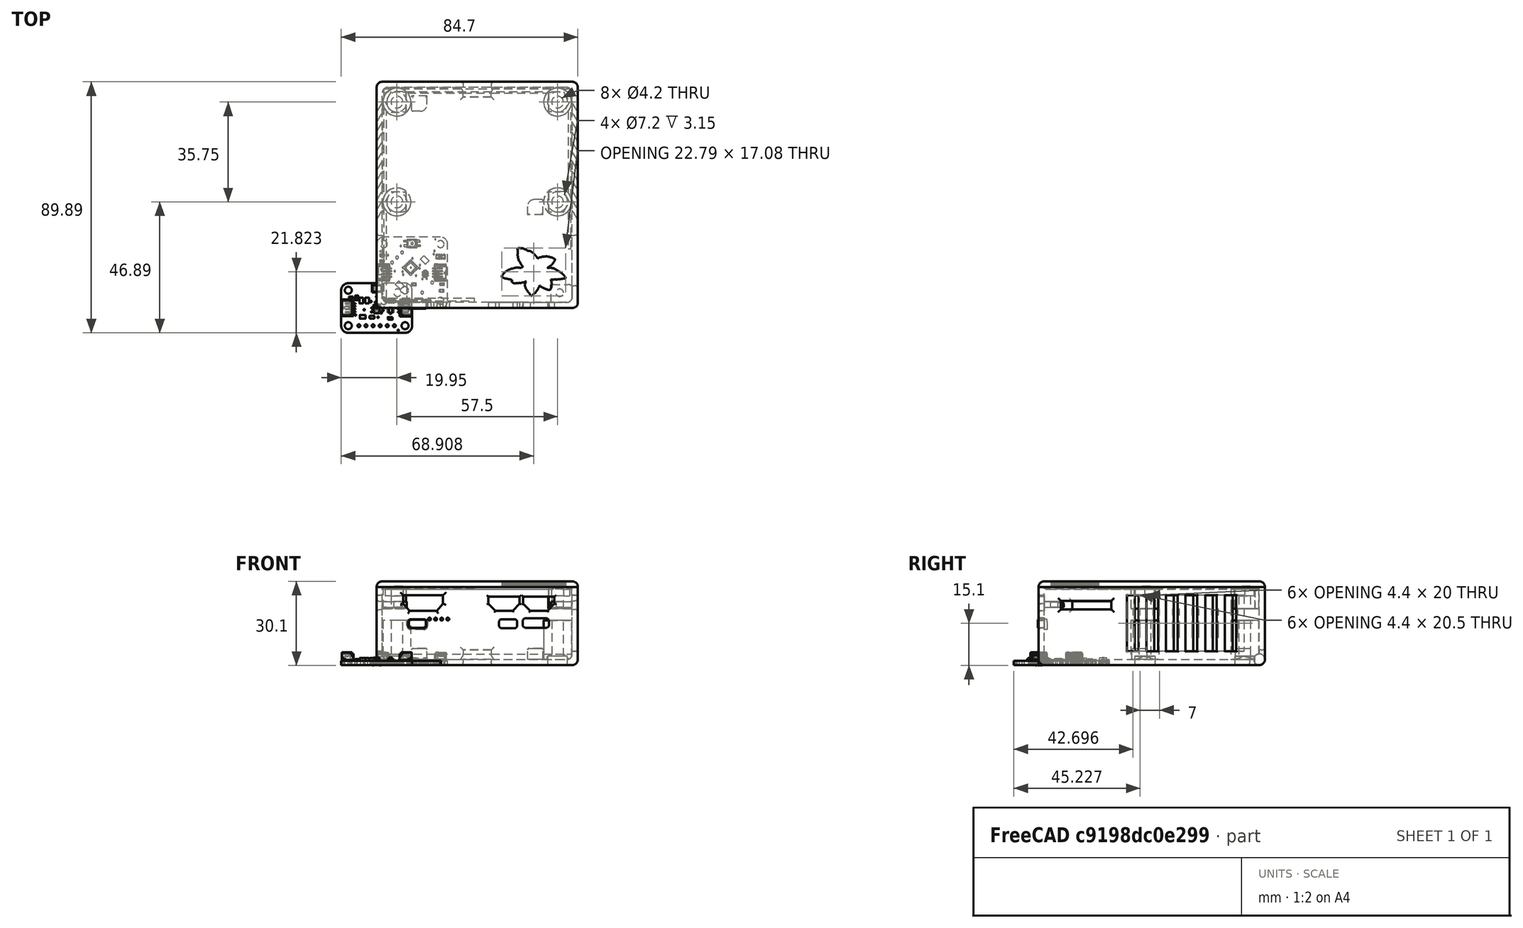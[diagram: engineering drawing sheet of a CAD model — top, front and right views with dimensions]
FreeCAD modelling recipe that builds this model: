
FCSTD DOCUMENT  (FreeCAD 0.20R29410 (Git))
Label: wearableV5_April_11_2023
License: All rights reserved
LicenseURL: http://en.wikipedia.org/wiki/All_rights_reserved
objects: Part::Feature×60, Part::Cylinder×20, Part::MultiFuse×16, Sketcher::SketchObject×15, Part::Extrusion×15, Part::Fillet×14, App::Part×9, Part::Box×5, Mesh::Feature×5, Part::Cut×4, Part::Compound×1
note: 150 computed .brp shape members not serialized (recipe doc carries the construction recipe); baked Part::Feature solids carry a one-line shape summary decoded from their .brp

FEATURE [Part::Box] Box  label="battery"
  AttacherType = Attacher::AttachEngine3D
  Height = 11
  Length = 65
  Placement = pos=(4,2,2) rot=(0,0,1;0rad)
  Width = 30
FEATURE [Mesh::Feature] pisugar3Board
  Placement = pos=(-2.89,35.08,0.25) rot=(-1,0,0;4.71239rad)
FEATURE [Part::Feature] Part__Feature001  label="RaspberryPiZeroW"
  Placement = pos=(36.5,17,19.18) rot=(1,0,0;1.5708rad)
  shape: bbox 65.9 x 31.25 x 4.8 mm, 368 faces, 2 solids (baked)
FEATURE [Part::Feature] Part__Feature  label="ips7100"
  Placement = pos=(-24,0,222) rot=(0.999993,-0.003655,0;3.14159rad)
  shape: bbox 48.14 x 14.05 x 44.14 mm, 1935 faces (baked)
FEATURE [Part::Compound] Compound  label="ips7100s"
  Links = -> [Part__Feature]
  Placement = pos=(12.15,32.5,15.79) rot=(0,0.707107,0.707107;3.15032rad)
FEATURE [Part::Feature] Part__Feature002  label="Printed Circuit Board"
  shape: bbox 25.4 x 17.78 x 1.6 mm, 42 faces (baked)
FEATURE [Part::Feature] Part__Feature003  label="EAHC2835WD6"
  shape: bbox 3.513 x 2.813 x 0.7485 mm, 108 faces, 4 solids (baked)
FEATURE [Part::Feature] Part__Feature004  label="AS7341 v2"
  Placement = pos=(0,-0.339822,1.6) rot=(0,0,1;0rad)
  shape: bbox 2 x 3.1 x 1.1 mm, 267 faces, 26 solids (baked)
FEATURE [Part::Feature] Part__Feature005  label="CAPC-0805-T0.95-BN v1"
  Placement = pos=(-5.01759,-3.15294,1.6) rot=(0,0,1;0rad)
  shape: bbox 2.1 x 1.35 x 0.95 mm, 42 faces (baked)
FEATURE [Part::Feature] Part__Feature006  label="CAPC-0805-T0.95-BN v002"
  Placement = pos=(-5.48627,2.66154,1.6) rot=(0,0,-1;1.5708rad)
  shape: bbox 1.35 x 2.1 x 0.95 mm, 42 faces (baked)
FEATURE [Part::Feature] Part__Feature007  label="CAPC-0805-T0.95-BN v003"
  Placement = pos=(-3.43627,2.66154,1.6) rot=(0,0,-1;1.5708rad)
  shape: bbox 1.35 x 2.1 x 0.95 mm, 42 faces (baked)
FEATURE [Part::Feature] Part__Feature008  label="CAPC-0603-T0.9-BN v1"
  Placement = pos=(-1.69987,-3.28475,1.6) rot=(0,0,1;0rad)
  shape: bbox 1.7 x 0.9 x 0.9 mm, 42 faces (baked)
FEATURE [Part::Feature] Part__Feature009  label="BODY_MF06A"
  Placement = pos=(0,0,0.762) rot=(0.57735,-0.57735,-0.57735;2.0944rad)
  shape: bbox 1.601 x 2.921 x 1.016 mm, 42 faces (baked)
FEATURE [Part::Feature] Part__Feature010  label="LEAD_MF06A"
  Placement = pos=(-0.9652,-0.9525,0.1016) rot=(0.57735,-0.57735,-0.57735;2.0944rad)
  shape: bbox 0.6223 x 0.3749 x 0.8636 mm, 14 faces (baked)
FEATURE [Part::Feature] Part__Feature011  label="LEAD_MF06A001"
  Placement = pos=(-0.9652,0,0.1016) rot=(0.57735,-0.57735,-0.57735;2.0944rad)
  shape: bbox 0.6223 x 0.3749 x 0.8636 mm, 14 faces (baked)
FEATURE [Part::Feature] Part__Feature012  label="LEAD_MF06A002"
  Placement = pos=(-0.9652,0.9525,0.1016) rot=(0.57735,-0.57735,-0.57735;2.0944rad)
  shape: bbox 0.6223 x 0.3749 x 0.8636 mm, 14 faces (baked)
FEATURE [Part::Feature] Part__Feature013  label="LEAD_MF06A003"
  Placement = pos=(0.9652,-0.9525,0.1016) rot=(0.57735,0.57735,0.57735;2.0944rad)
  shape: bbox 0.6223 x 0.3749 x 0.8636 mm, 14 faces (baked)
FEATURE [Part::Feature] Part__Feature014  label="LEAD_MF06A004"
  Placement = pos=(0.9652,0,0.1016) rot=(0.57735,0.57735,0.57735;2.0944rad)
  shape: bbox 0.6223 x 0.3749 x 0.8636 mm, 14 faces (baked)
FEATURE [Part::Feature] Part__Feature015  label="LEAD_MF06A005"
  Placement = pos=(0.9652,0.9525,0.1016) rot=(0.57735,0.57735,0.57735;2.0944rad)
  shape: bbox 0.6223 x 0.3749 x 0.8636 mm, 14 faces (baked)
FEATURE [Part::Feature] Part__Feature016  label="SOT363 v2"
  Placement = pos=(4.97054,-0.645171,1.675) rot=(0,0,1;3.14159rad)
  shape: bbox 2.1 x 2 x 1.1 mm, 94 faces, 7 solids (baked)
FEATURE [Part::Feature] Part__Feature017  label="LED 0603 single color v1"
  Placement = pos=(-9.18406,3.72778,1.60762) rot=(0,0,1;1.5708rad)
  shape: bbox 1.961 x 0.7932 x 0.7145 mm, 63 faces, 5 solids (baked)
FEATURE [Part::Feature] Part__Feature018  label="RESC-0603 v1"
  Placement = pos=(4.83432,-3.67461,1.6) rot=(0,0,1;0rad)
  shape: bbox 1.7 x 0.9 x 0.55 mm, 52 faces, 3 solids (baked)
FEATURE [Part::Feature] Part__Feature019  label="RESC-0603 v002"
  Placement = pos=(-7.14949,3.61248,1.6) rot=(0,0,-1;1.5708rad)
  shape: bbox 0.9 x 1.7 x 0.55 mm, 52 faces, 3 solids (baked)
FEATURE [Part::Feature] Part__Feature020  label="YC164_RESPACK v1"
  Placement = pos=(2.99591,1.52916,1.6) rot=(0,0,1;0rad)
  shape: bbox 3.2 x 1.6 x 0.61 mm, 172 faces (baked)
FEATURE [Part::Feature] Part__Feature021  label="qwicc v2"
  Placement = pos=(-10.8364,0.0607456,1.65) rot=(0,0,-1;1.5708rad)
  shape: bbox 4.95 x 6 x 2.96 mm, 229 faces, 7 solids (baked)
FEATURE [Part::Feature] Part__Feature022  label="qwicc v003"
  Placement = pos=(10.8256,0.00556102,1.65) rot=(0,0,1;1.5708rad)
  shape: bbox 4.95 x 6 x 2.96 mm, 229 faces, 7 solids (baked)
FEATURE [Part::Feature] Part__Feature023  label="scd30"
  Placement = pos=(20,54,27) rot=(0.57735,0.57735,-0.57735;4.18879rad)
  shape: bbox 23.02 x 35.11 x 7.027 mm, 2292 faces, 25 solids (baked)
FEATURE [App::Part] sot_23_6_v2  label="sot-23-6 v2"
  Group = -> [Part__Feature009,Part__Feature010,Part__Feature011,Part__Feature012,Part__Feature013,Part__Feature014,Part__Feature015]
  Origin = -> Origin
  Placement = pos=(-4.47945,-0.603742,1.69152) rot=(0,0,1;0rad)
FEATURE [App::Part] Adafruit_AS7341_STEMMA_QT_v2  label="bme280"
  Group = -> [Part__Feature002,Part__Feature003,Part__Feature004,Part__Feature005,Part__Feature006,Part__Feature007,Part__Feature008,sot_23_6_v2,Part__Feature016,Part__Feature017,Part__Feature018,Part__Feature019,Part__Feature020,Part__Feature021,Part__Feature022]
  Origin = -> Origin001
  Placement = pos=(47.7,42,20) rot=(0,0,1;0rad)
FEATURE [Part::Box] Box002  label="bottom"
  AttacherType = Attacher::AttachEngine3D
  Height = 28
  Length = 72
  Width = 81
FEATURE [Part::Fillet] Fillet  label="bottom002"
  Base = -> Box002
  Edges = 8 edges r=2: [Edge1,Edge3,Edge4,Edge5,Edge7,Edge8,Edge9,Edge11]
FEATURE [Part::Box] Box003  label="bottom001"
  AttacherType = Attacher::AttachEngine3D
  Height = 39
  Length = 68
  Placement = pos=(2,2,2) rot=(0,0,1;0rad)
  Width = 77
FEATURE [Part::Fillet] Fillet001  label="bottomCut"
  Base = -> Box003
  Edges = 8 edges r=2: [Edge1,Edge3,Edge4,Edge5,Edge7,Edge8,Edge9,Edge11]
FEATURE [Part::Cut] Cut  label="bottom003"
  Base = -> Fillet
  Tool = -> Fillet001
FEATURE [Part::Cylinder] Cylinder
  Angle = 360
  AttacherType = Attacher::AttachEngine3D
  FirstAngle = 0
  Height = 14
  Placement = pos=(7.25,73.75,2) rot=(0,0,1;0rad)
  Radius = 5
  SecondAngle = 0
FEATURE [Part::Cylinder] Cylinder001
  Angle = 360
  AttacherType = Attacher::AttachEngine3D
  FirstAngle = 0
  Height = 14
  Placement = pos=(64.75,38,2) rot=(0,0,1;0rad)
  Radius = 5
  SecondAngle = 0
FEATURE [Part::Cylinder] Cylinder002
  Angle = 360
  AttacherType = Attacher::AttachEngine3D
  FirstAngle = 0
  Height = 14
  Placement = pos=(7.25,38,2) rot=(0,0,1;0rad)
  Radius = 5
  SecondAngle = 0
FEATURE [Part::Cylinder] Cylinder003
  Angle = 360
  AttacherType = Attacher::AttachEngine3D
  FirstAngle = 0
  Height = 14
  Placement = pos=(64.75,73.75,2) rot=(0,0,1;0rad)
  Radius = 5
  SecondAngle = 0
FEATURE [Part::MultiFuse] Fusion  label="basesBottomIn"
  Shapes = -> [Cylinder003,Cylinder,Cylinder001,Cylinder002]
FEATURE [Part::Feature] Part__Feature024  label="Board"
  shape: bbox 25.4 x 25.4 x 1.57 mm, 211 faces (baked)
FEATURE [Part::Feature] Part__Feature025  label="QFN24_4MM"
  Placement = pos=(12.1412,14.4526,1.57) rot=(0,0,1;3.92699rad)
  shape: bbox 5.657 x 5.657 x 0.9 mm, 172 faces (baked)
FEATURE [Part::Feature] Part__Feature026  label="Part 5"
  shape: bbox 0.48 x 0.6603 x 0.6 mm, 14 faces (baked)
FEATURE [Part::Feature] Part__Feature027  label="Part 6"
  shape: bbox 0.48 x 0.6603 x 0.6 mm, 14 faces (baked)
FEATURE [Part::Feature] Part__Feature028  label="Part 4"
  shape: bbox 0.48 x 0.6603 x 0.6 mm, 14 faces (baked)
FEATURE [Part::Feature] Part__Feature029  label="Part 3"
  shape: bbox 0.48 x 0.6603 x 0.6 mm, 14 faces (baked)
FEATURE [Part::Feature] Part__Feature030  label="Part 2"
  shape: bbox 0.48 x 0.6603 x 0.6 mm, 14 faces (baked)
FEATURE [Part::Feature] Part__Feature031  label="Part 1"
  shape: bbox 3 x 1.4 x 1 mm, 10 faces (baked)
FEATURE [App::Part] _6700497  label="36700497"
  Group = -> [Part__Feature026,Part__Feature027,Part__Feature028,Part__Feature029,Part__Feature030,Part__Feature031]
  Origin = -> Origin002
  Placement = pos=(0,0,0) rot=(0,0,1;3.14159rad)
FEATURE [App::Part] SOT23_5  label="SOT23-5"
  Group = -> [_6700497]
  Origin = -> Origin003
  Placement = pos=(2.54,6.985,1.57) rot=(0,0,1;3.14159rad)
FEATURE [Part::Feature] Part__Feature032  label="Pin1"
  shape: bbox 0.6224 x 1.252 x 1.252 mm, 37 faces (baked)
FEATURE [Part::Feature] Part__Feature033  label="Pin2"
  shape: bbox 0.6224 x 1.252 x 1.252 mm, 37 faces (baked)
FEATURE [Part::Feature] Part__Feature034  label="CeramicBody"
  shape: bbox 1.8 x 1.23 x 1.23 mm, 10 faces (baked)
FEATURE [App::Part] _603_NO  label="0603-NO"
  Group = -> [Part__Feature032,Part__Feature033,Part__Feature034]
  Origin = -> Origin004
  Placement = pos=(16.51,8.382,1.57) rot=(0,0,1;0rad)
FEATURE [Part::Feature] Part__Feature035  label="0603-NO (1)"
  Placement = pos=(23.241,6.223,1.57) rot=(0,0,1;0rad)
  shape: bbox 1.7 x 0.9 x 0.55 mm, 52 faces, 3 solids (baked)
FEATURE [Part::Feature] Part__Feature036  label="0603-NO (2)"
  Placement = pos=(13.3858,8.4328,1.57) rot=(0,0,1;0rad)
  shape: bbox 1.7 x 0.9 x 0.55 mm, 52 faces, 3 solids (baked)
FEATURE [Part::Feature] Part__Feature037  label="0603-NO (3)"
  Placement = pos=(1.905,18.923,1.57) rot=(0,0,1;3.14159rad)
  shape: bbox 1.7 x 0.9 x 0.55 mm, 52 faces, 3 solids (baked)
FEATURE [Part::Feature] Part__Feature038  label="Pin1 (1)"
  shape: bbox 0.6224 x 1.252 x 1.252 mm, 37 faces (baked)
FEATURE [Part::Feature] Part__Feature039  label="Pin2 (1)"
  shape: bbox 0.6224 x 1.252 x 1.252 mm, 37 faces (baked)
FEATURE [Part::Feature] Part__Feature040  label="CeramicBody (1)"
  shape: bbox 1.8 x 1.23 x 1.23 mm, 10 faces (baked)
FEATURE [App::Part] _805_NO  label="0805-NO"
  Group = -> [Part__Feature038,Part__Feature039,Part__Feature040]
  Origin = -> Origin005
  Placement = pos=(7.874,13.589,1.57) rot=(0,0,1;1.5708rad)
FEATURE [Part::Feature] Part__Feature041  label="Pin1 (2)"
  shape: bbox 0.6224 x 1.252 x 1.252 mm, 37 faces (baked)
FEATURE [Part::Feature] Part__Feature042  label="Pin2 (2)"
  shape: bbox 0.6224 x 1.252 x 1.252 mm, 37 faces (baked)
FEATURE [Part::Feature] Part__Feature043  label="CeramicBody (2)"
  shape: bbox 1.8 x 1.23 x 1.23 mm, 10 faces (baked)
FEATURE [App::Part] _805_NO__1_  label="0805-NO (1)"
  Group = -> [Part__Feature041,Part__Feature042,Part__Feature043]
  Origin = -> Origin006
  Placement = pos=(12.827,6.223,1.57) rot=(0,0,1;3.14159rad)
FEATURE [Part::Feature] Part__Feature044  label="CHIPLED_0603_NOOUTLINE"
  Placement = pos=(23.368,8.509,1.57) rot=(0,0,1;1.5708rad)
  shape: bbox 1.616 x 0.8 x 0.4 mm, 133 faces (baked)
FEATURE [Part::Feature] Part__Feature045  label="CHIPLED_0603_NOOUTLINE (1)"
  Placement = pos=(1.905,16.764,1.57) rot=(0,0,-1;1.5708rad)
  shape: bbox 1.616 x 0.8 x 0.4 mm, 133 faces (baked)
FEATURE [Part::Feature] Part__Feature046  label="JST_SH4"
  Placement = pos=(22.86,12.7,1.57) rot=(0,0,1;1.5708rad)
  shape: bbox 4.95 x 6 x 2.96 mm, 229 faces, 7 solids (baked)
FEATURE [Part::Feature] Part__Feature047  label="JST_SH4 (1)"
  Placement = pos=(2.54,12.7,1.57) rot=(0,0,-1;1.5708rad)
  shape: bbox 4.95 x 6 x 2.96 mm, 229 faces, 7 solids (baked)
FEATURE [Part::Feature] Part__Feature048  label="NEO3535_REVERSE"
  Placement = pos=(12.7,23.114,0) rot=(0,1,0;3.14159rad)
  shape: bbox 5.88 x 2.8 x 1.78 mm, 41 faces, 5 solids (baked)
FEATURE [Part::Feature] Part__Feature049  label="RESPACK_4X0603"
  Placement = pos=(22.86,18.415,1.57) rot=(0,0,1;3.14159rad)
  shape: bbox 3.2 x 1.6 x 0.61 mm, 172 faces (baked)
FEATURE [Part::Feature] Part__Feature050  label="SOT363"
  Placement = pos=(17.399,12.192,1.57) rot=(0,0,-1;1.5708rad)
  shape: bbox 2.208 x 2.208 x 1.121 mm, 178 faces, 4 solids (baked)
FEATURE [App::Part] Packages
  Group = -> [Part__Feature025,SOT23_5,_603_NO,Part__Feature035,Part__Feature036,Part__Feature037,_805_NO,_805_NO__1_,Part__Feature044,Part__Feature045,Part__Feature046,Part__Feature047,Part__Feature048,Part__Feature049,Part__Feature050]
  Origin = -> Origin007
FEATURE [App::Part] Adafruit_I2C_QT_Rotary_Encoder_v2  label="gps"
  Group = -> [Part__Feature024,Packages]
  Origin = -> Origin008
  Placement = pos=(35,51,20) rot=(0,0,1;0rad)
FEATURE [Part::Cylinder] Cylinder004
  Angle = 360
  AttacherType = Attacher::AttachEngine3D
  FirstAngle = 0
  Height = 14
  Placement = pos=(7.25,73.75,2) rot=(0,0,1;0rad)
  Radius = 2.1
  SecondAngle = 0
FEATURE [Part::Cylinder] Cylinder005
  Angle = 360
  AttacherType = Attacher::AttachEngine3D
  FirstAngle = 0
  Height = 14
  Placement = pos=(64.75,38,2) rot=(0,0,1;0rad)
  Radius = 2.1
  SecondAngle = 0
FEATURE [Part::Cylinder] Cylinder006
  Angle = 360
  AttacherType = Attacher::AttachEngine3D
  FirstAngle = 0
  Height = 14
  Placement = pos=(7.25,38,2) rot=(0,0,1;0rad)
  Radius = 2.1
  SecondAngle = 0
FEATURE [Part::Cylinder] Cylinder007
  Angle = 360
  AttacherType = Attacher::AttachEngine3D
  FirstAngle = 0
  Height = 14
  Placement = pos=(64.75,73.75,2) rot=(0,0,1;0rad)
  Radius = 2.1
  SecondAngle = 0
FEATURE [Part::MultiFuse] Fusion001  label="basesM4BottomCuts"
  Shapes = -> [Cylinder007,Cylinder004,Cylinder005,Cylinder006]
FEATURE [Sketcher::SketchObject] Sketch
  FullyConstrained = true
  expr: Constraints[40] = 69.75
  sketch-geometry (41):
    g0: LineSegment StartX=2.25 StartY=43 StartZ=0 EndX=2.25 EndY=33 EndZ=0
    g1: LineSegment StartX=2.25 StartY=33 StartZ=0 EndX=69.75 EndY=33 EndZ=0
    g2: LineSegment StartX=2.25 StartY=43 StartZ=0 EndX=8.25 EndY=43 EndZ=0
    g3: LineSegment StartX=2.25 StartY=70 StartZ=0 EndX=8.25 EndY=70 EndZ=0
    g4: LineSegment StartX=2.25 StartY=70 StartZ=0 EndX=2.25 EndY=77 EndZ=0
    g5: ArcOfCircle CenterX=4 CenterY=77 CenterZ=0 NormalX=0 NormalY=0 NormalZ=1 AngleXU=0 Radius=1.75 StartAngle=1.5708 EndAngle=3.14159
    g6: LineSegment StartX=4 StartY=78.75 StartZ=0 EndX=68 EndY=78.75 EndZ=0
    g7: ArcOfCircle CenterX=68 CenterY=77 CenterZ=0 NormalX=0 NormalY=0 NormalZ=1 AngleXU=0 Radius=1.75 StartAngle=1.61e-14 EndAngle=1.5708
    g8: LineSegment StartX=69.75 StartY=77 StartZ=0 EndX=69.75 EndY=70 EndZ=0
    g9: LineSegment StartX=69.75 StartY=70 StartZ=0 EndX=63.75 EndY=70 EndZ=0
    g10: LineSegment StartX=63.75 StartY=70 StartZ=0 EndX=63.75 EndY=43 EndZ=0
    g11: LineSegment StartX=63.75 StartY=43 StartZ=0 EndX=69.75 EndY=43 EndZ=0
    g12: LineSegment StartX=69.75 StartY=43 StartZ=0 EndX=69.75 EndY=33 EndZ=0
    g13: GeomPoint X=69.75 Y=33 Z=0
    g14: GeomPoint X=69.75 Y=33 Z=0
    g15: GeomPoint X=69.75 Y=33 Z=0
    g16: GeomPoint X=69.75 Y=33 Z=0
    g17: GeomPoint X=69.75 Y=33 Z=0
    g18: LineSegment StartX=8.25 StartY=43 StartZ=0 EndX=8.25 EndY=70 EndZ=0
    g19: Circle CenterX=7.25 CenterY=73.75 CenterZ=0 NormalX=0 NormalY=0 NormalZ=1 AngleXU=0 Radius=2.1
    g20: Circle CenterX=7.25 CenterY=38 CenterZ=0 NormalX=0 NormalY=0 NormalZ=1 AngleXU=0 Radius=2.1
    g21: Circle CenterX=64.75 CenterY=38 CenterZ=0 NormalX=0 NormalY=0 NormalZ=1 AngleXU=0 Radius=2.1
    g22: Circle CenterX=64.75 CenterY=73.75 CenterZ=0 NormalX=0 NormalY=0 NormalZ=1 AngleXU=0 Radius=2.1
    g23: Circle CenterX=13.2 CenterY=71.45 CenterZ=0 NormalX=0 NormalY=0 NormalZ=1 AngleXU=0 Radius=1.6
    g24: Circle CenterX=37.54 CenterY=73.86 CenterZ=0 NormalX=0 NormalY=0 NormalZ=1 AngleXU=0 Radius=1.6
    g25: Circle CenterX=57.86 CenterY=73.86 CenterZ=0 NormalX=0 NormalY=0 NormalZ=1 AngleXU=0 Radius=1.6
    g26: Circle CenterX=37.54 CenterY=53.54 CenterZ=0 NormalX=0 NormalY=0 NormalZ=1 AngleXU=0 Radius=1.6
    g27: Circle CenterX=57.86 CenterY=53.54 CenterZ=0 NormalX=0 NormalY=0 NormalZ=1 AngleXU=0 Radius=1.6
    g28: Circle CenterX=37.54 CenterY=48.35 CenterZ=0 NormalX=0 NormalY=0 NormalZ=1 AngleXU=0 Radius=1.6
    g29: Circle CenterX=57.86 CenterY=48.35 CenterZ=0 NormalX=0 NormalY=0 NormalZ=1 AngleXU=0 Radius=1.6
    g30: Circle CenterX=37.54 CenterY=35.65 CenterZ=0 NormalX=0 NormalY=0 NormalZ=1 AngleXU=0 Radius=1.6
    g31: Circle CenterX=57.86 CenterY=35.65 CenterZ=0 NormalX=0 NormalY=0 NormalZ=1 AngleXU=0 Radius=1.6
    g32: Circle CenterX=29.425 CenterY=39.45 CenterZ=0 NormalX=0 NormalY=0 NormalZ=1 AngleXU=0 Radius=1.6
    g33: ArcOfCircle CenterX=46.7 CenterY=66.86 CenterZ=0 NormalX=0 NormalY=0 NormalZ=1 AngleXU=0 Radius=5 StartAngle=2e-16 EndAngle=3.14159
    g34: ArcOfCircle CenterX=46.7 CenterY=42.65 CenterZ=0 NormalX=0 NormalY=0 NormalZ=1 AngleXU=0 Radius=5 StartAngle=3.14159 EndAngle=6.28319
    g35: LineSegment StartX=41.7 StartY=66.86 StartZ=0 EndX=41.7 EndY=42.65 EndZ=0
    g36: LineSegment StartX=51.7 StartY=42.65 StartZ=0 EndX=51.7 EndY=66.86 EndZ=0
    g37: ArcOfCircle CenterX=21.2 CenterY=66.86 CenterZ=0 NormalX=0 NormalY=0 NormalZ=1 AngleXU=0 Radius=5 StartAngle=0 EndAngle=3.14159
    g38: ArcOfCircle CenterX=21.2 CenterY=42.65 CenterZ=0 NormalX=0 NormalY=0 NormalZ=1 AngleXU=0 Radius=5 StartAngle=3.14159 EndAngle=6.28319
    g39: LineSegment StartX=16.2 StartY=66.86 StartZ=0 EndX=16.2 EndY=42.65 EndZ=0
    g40: LineSegment StartX=26.2 StartY=42.65 StartZ=0 EndX=26.2 EndY=66.86 EndZ=0
  constraints (111):
    c: Vertical(g0)
    c: Coincident(g1,g0)
    c: Horizontal(g1)
    c: Coincident(g2,g0)
    c: Coincident(g4,g3)
    c: Vertical(g4)
    c: Coincident(g5,g4)
    c: Horizontal(g6)
    c: Coincident(g7,g6)
    c: Coincident(g8,g7)
    c: Coincident(g9,g8)
    c: Horizontal(g9)
    c: Coincident(g10,g9)
    c: Vertical(g10)
    c: Horizontal(g11)
    c: DistanceX(g-1,g0) = 2.25
    c: Horizontal(g2)
    c: Coincident(g13,g12)
    c: Coincident(g14,g1)
    c: Coincident(g15,g12)
    c: Coincident(g16,g1)
    c: Coincident(g17,g12)
    c: Coincident(g12,g1)
    c: Vertical(g12)
    c: Coincident(g5,g6)
    c: Coincident(g18,g2)
    c: Coincident(g18,g3)
    c: Vertical(g18)
    c: Horizontal(g3)
    c: Vertical(g8)
    c: DistanceY(g0) = 33
    c: DistanceX(g0,g2) = 6
    c: DistanceY(g0,g0) = 10
    c: DistanceX(g3,g3) = 6
    c: DistanceY(g18,g18) = 27
    c: DistanceY(g4,g4) = 7
    c: DistanceY(g5) = 77
    c: Angle(g5) = 1.5708
    c: Radius(g7) = 1.75
    c: Angle(g7) = 1.5708
    c: DistanceX(g1) = 69.75
    c: Coincident(g11,g12)
    c: DistanceY(g1,g11) = 10
    c: Coincident(g10,g11)
    c: DistanceX(g11,g11) = 6
    c: DistanceX(g6,g6) = 64
    c: Radius(g19) = 2.1
    c: DistanceX(g20) = 7.25
    c: DistanceY(g20) = 38
    c: Radius(g20) = 2.1
    c: DistanceX(g21) = 64.75
    c: DistanceY(g20,g21) = 0
    c: Radius(g21) = 2.1
    c: DistanceX(g22,g21) = 0
    c: Radius(g22) = 2.1
    c: DistanceX(g19,g22) = 57.5
    c: DistanceY(g19) = 73.75
    c: DistanceY(g19,g22) = 0
    c: DistanceY(g3,g8) = 0
    c: DistanceX(g5) = 4
    c: DistanceX(g24) = 37.54
    c: Radius(g24) = 1.6
    c: DistanceY(g24,g25) = 0
    c: Radius(g25) = 1.6
    c: DistanceX(g24,g25) = 20.32
    c: DistanceY(g24) = 73.86
    c: DistanceX(g26,g24) = 0
    c: Radius(g26) = 1.6
    c: DistanceY(g26,g24) = 20.32
    c: DistanceY(g27,g26) = 0
    c: DistanceX(g27,g25) = 0
    c: Radius(g27) = 1.6
    c: DistanceX(g28,g26) = 0
    c: DistanceY(g28) = 48.35
    c: Radius(g28) = 1.6
    c: DistanceY(g28,g29) = 0
    c: DistanceX(g27,g29) = 0
    c: Radius(g29) = 1.6
    c: DistanceX(g28,g30) = 0
    c: DistanceX(g31,g29) = 0
    c: DistanceY(g30,g28) = 12.7
    c: DistanceY(g31,g30) = 0
    c: Radius(g31) = 1.6
    c: Radius(g30) = 1.6
    c: Radius(g32) = 1.6
    c: DistanceY(g32) = 39.45
    c: DistanceX(g32) = 29.425
    c: DistanceY(g32,g23) = 32
    c: DistanceX(g23,g32) = 16.225
    c: Radius(g23) = 1.6
    c: Tangent(g33,g35) = -1.5708
    c: Tangent(g35,g34) = -1.5708
    c: Tangent(g34,g36) = -1.5708
    c: Tangent(g36,g33) = -1.5708
    c: Equal(g33,g34)
    c: Vertical(g35)
    c: DistanceX(g33) = 46.7
    c: DistanceY(g33,g24) = 7
    c: DistanceY(g30,g34) = 7
    c: Radius(g33) = 5
    c: Tangent(g37,g39) = -1.5708
    c: Tangent(g39,g38) = -1.5708
    c: Tangent(g38,g40) = -1.5708
    c: Tangent(g40,g37) = -1.5708
    c: Equal(g37,g38)
    c: Vertical(g39)
    c: Radius(g37) = 5
    c: DistanceY(g37,g33) = 0
    c: DistanceY(g34,g38) = 0
    c: DistanceX(g23,g37) = 8
    c: DistanceY(g8,g8) = 7
FEATURE [Part::Extrusion] Extrude  label="sensorHold"
  Base = -> Sketch
  Dir = (0,0,1)
  DirMode = 2
  FaceMakerClass = Part::FaceMakerBullseye
  LengthFwd = 4
  LengthRev = 0
  Placement = pos=(0,0,16) rot=(0,0,1;0rad)
  Solid = true
  Symmetric = false
FEATURE [Part::Fillet] Fillet002  label="sensorHold001"
  Base = -> Extrude
  Edges = 10 edges r=2: [Edge1,Edge2,Edge5,Edge8,Edge11,Edge14,Edge17,Edge20,Edge35,Edge38]
FEATURE [Sketcher::SketchObject] Sketch001
  FullyConstrained = true
  sketch-geometry (10):
    g0: LineSegment StartX=18.03 StartY=72.94 StartZ=0 EndX=18.03 EndY=75.94 EndZ=0
    g1: LineSegment StartX=15.53 StartY=70.44 StartZ=0 EndX=12.53 EndY=70.44 EndZ=0
    g2: LineSegment StartX=12.53 StartY=70.44 StartZ=0 EndX=12.53 EndY=75.94 EndZ=0
    g3: LineSegment StartX=18.03 StartY=75.94 StartZ=0 EndX=12.53 EndY=75.94 EndZ=0
    g4: ArcOfCircle CenterX=15.53 CenterY=72.94 CenterZ=0 NormalX=0 NormalY=0 NormalZ=1 AngleXU=0 Radius=2.5 StartAngle=4.71239 EndAngle=6.28319
    g5: LineSegment StartX=59.53 StartY=33.36 StartZ=0 EndX=54.03 EndY=33.36 EndZ=0
    g6: LineSegment StartX=54.03 StartY=33.36 StartZ=0 EndX=54.03 EndY=36.36 EndZ=0
    g7: LineSegment StartX=59.53 StartY=33.36 StartZ=0 EndX=59.53 EndY=38.86 EndZ=0
    g8: LineSegment StartX=59.53 StartY=38.86 StartZ=0 EndX=56.53 EndY=38.86 EndZ=0
    g9: ArcOfCircle CenterX=56.53 CenterY=36.36 CenterZ=0 NormalX=0 NormalY=0 NormalZ=1 AngleXU=0 Radius=2.5 StartAngle=1.5708 EndAngle=3.14159
  constraints (32):
    c: Vertical(g0)
    c: Horizontal(g1)
    c: Vertical(g2)
    c: Coincident(g2,g3)
    c: Coincident(g0,g3)
    c: Horizontal(g3)
    c: DistanceX(g3,g3) = 5.5
    c: DistanceY(g2,g2) = 5.5
    c: DistanceY(g4,g4) = 0
    c: DistanceX(g4,g4) = 0
    c: Coincident(g1,g4)
    c: Coincident(g0,g4)
    c: Radius(g4) = 2.5
    c: DistanceX(g4) = 15.53
    c: DistanceY(g4) = 72.94
    c: Coincident(g1,g2)
    c: Horizontal(g5)
    c: Vertical(g6)
    c: Vertical(g7)
    c: Horizontal(g8)
    c: Coincident(g7,g8)
    c: Coincident(g8,g9)
    c: Coincident(g6,g9)
    c: Coincident(g5,g6)
    c: Coincident(g5,g7)
    c: DistanceX(g5,g5) = 5.5
    c: DistanceY(g7,g7) = 5.5
    c: DistanceY(g6,g6) = 3
    c: DistanceX(g8,g8) = 3
    c: Radius(g9) = 2.5
    c: DistanceY(g9,g4) = 36.58
    c: DistanceX(g4,g9) = 41
FEATURE [Part::Extrusion] Extrude001
  Base = -> Sketch001
  Dir = (0,0,1)
  DirMode = 2
  FaceMakerClass = Part::FaceMakerBullseye
  LengthFwd = 4
  LengthRev = 0
  Placement = pos=(0,0,2) rot=(0,0,1;0rad)
  Solid = true
  Symmetric = false
FEATURE [Part::Fillet] Fillet003  label="ipsHoldBottomIn"
  Base = -> Extrude001
  Edges = 14 edges r=0.5: [Edge4,Edge7,Edge10,Edge11,Edge13,Edge15,Edge19,Edge20,Edge22,Edge23,Edge25,Edge26,Edge28,Edge30]
FEATURE [Sketcher::SketchObject] Sketch002
  FullyConstrained = true
  MapMode = 2
  Support = -> [Cut]
  sketch-geometry (10):
    g0: LineSegment StartX=62.5 StartY=8.4 StartZ=0 EndX=70.5 EndY=8.4 EndZ=0
    g1: LineSegment StartX=70.5 StartY=8.4 StartZ=0 EndX=70.5 EndY=1.5 EndZ=0
    g2: LineSegment StartX=70.5 StartY=1.5 StartZ=0 EndX=62.5 EndY=1.5 EndZ=0
    g3: LineSegment StartX=62.5 StartY=1.5 StartZ=0 EndX=62.5 EndY=8.4 EndZ=0
    g4: LineSegment StartX=1.5 StartY=9 StartZ=0 EndX=10.75 EndY=9 EndZ=0
    g5: LineSegment StartX=10.75 StartY=9 StartZ=0 EndX=10.75 EndY=1.5 EndZ=0
    g6: LineSegment StartX=10.75 StartY=1.5 StartZ=0 EndX=1.5 EndY=1.5 EndZ=0
    g7: LineSegment StartX=1.5 StartY=1.5 StartZ=0 EndX=1.5 EndY=9 EndZ=0
    g8: Circle CenterX=7.47 CenterY=5.475 CenterZ=0 NormalX=0 NormalY=0 NormalZ=1 AngleXU=0 Radius=1.35
    g9: Circle CenterX=65.52 CenterY=5.475 CenterZ=0 NormalX=0 NormalY=0 NormalZ=1 AngleXU=0 Radius=1.35
  constraints (30):
    c: Coincident(g0,g1)
    c: Coincident(g1,g2)
    c: Coincident(g2,g3)
    c: Coincident(g3,g0)
    c: Horizontal(g0)
    c: Horizontal(g2)
    c: Vertical(g1)
    c: Vertical(g3)
    c: Coincident(g4,g5)
    c: Coincident(g5,g6)
    c: Coincident(g6,g7)
    c: Coincident(g7,g4)
    c: Horizontal(g4)
    c: Horizontal(g6)
    c: Vertical(g5)
    c: Vertical(g7)
    c: DistanceX(g6) = 1.5
    c: DistanceY(g6) = 1.5
    c: DistanceX(g6,g6) = 9.25
    c: DistanceY(g7,g7) = 7.5
    c: DistanceX(g-1,g1) = 70.5
    c: DistanceY(g2,g5) = 0
    c: DistanceY(g0,g4) = 0.6
    c: DistanceX(g2,g2) = 8
    c: DistanceX(g8) = 7.47
    c: Radius(g8) = 1.35
    c: DistanceX(g9) = 65.52
    c: DistanceY(g8,g9) = 0
    c: Radius(g9) = 1.35
    c: DistanceY(g8) = 5.475
FEATURE [Part::Extrusion] Extrude002  label="RaberryPiHold"
  Base = -> Sketch002
  Dir = (0,0,1)
  DirMode = 2
  FaceMakerClass = Part::FaceMakerBullseye
  LengthFwd = 2
  LengthRev = 0
  Placement = pos=(0,0,20.7) rot=(0,0,1;0rad)
  Solid = true
  Symmetric = false
FEATURE [Part::Fillet] Fillet004  label="piHoldBottomIn"
  Base = -> Extrude002
  Edges = 6 edges: [Edge1 r=2,Edge4 r=1,Edge12 r=1,Edge17 r=2,Edge19 r=1,Edge22 r=1]
FEATURE [Part::Box] Box004  label="top"
  AttacherType = Attacher::AttachEngine3D
  Height = 2
  Length = 72
  Placement = pos=(0,0,28) rot=(0,0,1;0rad)
  Width = 81
FEATURE [Part::Fillet] Fillet005  label="top001"
  Base = -> Box004
  Edges = 8 edges r=1.95: [Edge1,Edge2,Edge3,Edge5,Edge6,Edge7,Edge10,Edge12]
FEATURE [Part::Feature] Part__Feature052  label="m4s"
  Placement = pos=(64.75,73.75,14) rot=(1,0,0;3.14159rad)
  shape: bbox 5.501 x 5.501 x 28.29 mm, 108 faces (baked)
FEATURE [Part::Feature] Part__Feature053  label="m4s001"
  Placement = pos=(7.25,73.75,14) rot=(1,0,0;3.14159rad)
  shape: bbox 5.501 x 5.501 x 28.29 mm, 108 faces (baked)
FEATURE [Part::Feature] Part__Feature054  label="m4s002"
  Placement = pos=(64.75,38,14) rot=(1,0,0;3.14159rad)
  shape: bbox 5.501 x 5.501 x 28.29 mm, 108 faces (baked)
FEATURE [Part::Feature] Part__Feature055  label="m4s003"
  Placement = pos=(7.25,38,14) rot=(1,0,0;3.14159rad)
  shape: bbox 5.501 x 5.501 x 28.29 mm, 108 faces (baked)
FEATURE [Part::Cylinder] Cylinder008
  Angle = 360
  AttacherType = Attacher::AttachEngine3D
  FirstAngle = 0
  Height = 7.75
  Placement = pos=(7.25,73.75,2) rot=(0,0,1;0rad)
  Radius = 5
  SecondAngle = 0
FEATURE [Part::Cylinder] Cylinder009
  Angle = 360
  AttacherType = Attacher::AttachEngine3D
  FirstAngle = 0
  Height = 7.75
  Placement = pos=(64.75,38,2) rot=(0,0,1;0rad)
  Radius = 5
  SecondAngle = 0
FEATURE [Part::Cylinder] Cylinder010
  Angle = 360
  AttacherType = Attacher::AttachEngine3D
  FirstAngle = 0
  Height = 7.75
  Placement = pos=(7.25,38,2) rot=(0,0,1;0rad)
  Radius = 5
  SecondAngle = 0
FEATURE [Part::Cylinder] Cylinder011
  Angle = 360
  AttacherType = Attacher::AttachEngine3D
  FirstAngle = 0
  Height = 7.75
  Placement = pos=(64.75,73.75,2) rot=(0,0,1;0rad)
  Radius = 5
  SecondAngle = 0
FEATURE [Part::Feature] Part__Feature056  label="m4Nut"
  Placement = pos=(7.25,38,27) rot=(0,0,1;1.5708rad)
  shape: bbox 8.084 x 8.084 x 2.714 mm, 34 faces (baked)
FEATURE [Part::MultiFuse] Fusion003  label="m4s004"
  Shapes = -> [Part__Feature055,Part__Feature052,Part__Feature053,Part__Feature054]
FEATURE [Part::Feature] Part__Feature057  label="m4Nut001"
  Placement = pos=(64.75,38,27) rot=(0,0,1;1.5708rad)
  shape: bbox 8.084 x 8.084 x 2.714 mm, 34 faces (baked)
FEATURE [Part::MultiFuse] Fusion004
  Shapes = -> [Part__Feature056,Part__Feature057]
FEATURE [Part::Feature] Part__Feature058  label="m4Nut002"
  Placement = pos=(7.25,38,27) rot=(0,0,1;1.5708rad)
  shape: bbox 8.084 x 8.084 x 2.714 mm, 34 faces (baked)
FEATURE [Part::Feature] Part__Feature059  label="m4Nut003"
  Placement = pos=(64.75,38,27) rot=(0,0,1;1.5708rad)
  shape: bbox 8.084 x 8.084 x 2.714 mm, 34 faces (baked)
FEATURE [Part::MultiFuse] Fusion005
  Placement = pos=(0,35.75,0) rot=(0,0,1;0rad)
  Shapes = -> [Part__Feature058,Part__Feature059]
FEATURE [Part::MultiFuse] Fusion006  label="m4Nuts"
  Placement = pos=(0,0,-1) rot=(0,0,1;0rad)
  Shapes = -> [Fusion005,Fusion004]
FEATURE [Sketcher::SketchObject] Sketch003
  FullyConstrained = true
  MapMode = 2
  Placement = pos=(70,0,30) rot=(0,1,0;3.14159rad)
  sketch-geometry (36):
    g0: LineSegment StartX=3.125 StartY=34.3194 StartZ=0 EndX=7.375 EndY=34.3194 EndZ=0
    g1: LineSegment StartX=7.375 StartY=34.3194 StartZ=0 EndX=7.47604 EndY=34.4944 EndZ=0
    g2: LineSegment StartX=3.125 StartY=34.3194 StartZ=0 EndX=1 EndY=38 EndZ=0
    g3: LineSegment StartX=1 StartY=38 StartZ=0 EndX=3.125 EndY=41.6806 EndZ=0
    g4: LineSegment StartX=3.125 StartY=41.6806 StartZ=0 EndX=7.375 EndY=41.6806 EndZ=0
    g5: LineSegment StartX=7.375 StartY=41.6806 StartZ=0 EndX=7.47604 EndY=41.5056 EndZ=0
    g6: LineSegment StartX=7.47604 StartY=41.5056 StartZ=0 EndX=10.476 EndY=41.5056 EndZ=0
    g7: LineSegment StartX=10.476 StartY=41.5056 StartZ=0 EndX=10.476 EndY=34.4944 EndZ=0
    g8: LineSegment StartX=10.476 StartY=34.4944 StartZ=0 EndX=7.47604 EndY=34.4944 EndZ=0
    g9: LineSegment StartX=60.524 StartY=34.4944 StartZ=0 EndX=60.625 EndY=34.3194 EndZ=0
    g10: LineSegment StartX=60.625 StartY=34.3194 StartZ=0 EndX=64.875 EndY=34.3194 EndZ=0
    g11: LineSegment StartX=64.875 StartY=34.3194 StartZ=0 EndX=67 EndY=38 EndZ=0
    g12: LineSegment StartX=67 StartY=38 StartZ=0 EndX=64.875 EndY=41.6806 EndZ=0
    g13: LineSegment StartX=64.875 StartY=41.6806 StartZ=0 EndX=60.625 EndY=41.6806 EndZ=0
    g14: LineSegment StartX=60.625 StartY=41.6806 StartZ=0 EndX=60.524 EndY=41.5056 EndZ=0
    g15: LineSegment StartX=60.524 StartY=41.5056 StartZ=0 EndX=57.524 EndY=41.5056 EndZ=0
    g16: LineSegment StartX=57.524 StartY=41.5056 StartZ=0 EndX=57.524 EndY=34.4944 EndZ=0
    g17: LineSegment StartX=57.524 StartY=34.4944 StartZ=0 EndX=60.524 EndY=34.4944 EndZ=0
    g18: LineSegment StartX=1 StartY=73.75 StartZ=0 EndX=3.125 EndY=70.0694 EndZ=0
    g19: LineSegment StartX=3.125 StartY=70.0694 StartZ=0 EndX=7.375 EndY=70.0694 EndZ=0
    g20: LineSegment StartX=7.375 StartY=70.0694 StartZ=0 EndX=7.47604 EndY=70.2444 EndZ=0
    g21: LineSegment StartX=7.47604 StartY=70.2444 StartZ=0 EndX=10.476 EndY=70.2444 EndZ=0
    g22: LineSegment StartX=10.476 StartY=70.2444 StartZ=0 EndX=10.476 EndY=77.2556 EndZ=0
    g23: LineSegment StartX=10.476 StartY=77.2556 StartZ=0 EndX=7.47604 EndY=77.2556 EndZ=0
    g24: LineSegment StartX=7.47604 StartY=77.2556 StartZ=0 EndX=7.375 EndY=77.4306 EndZ=0
    g25: LineSegment StartX=7.375 StartY=77.4306 StartZ=0 EndX=3.125 EndY=77.4306 EndZ=0
    g26: LineSegment StartX=3.125 StartY=77.4306 StartZ=0 EndX=1 EndY=73.75 EndZ=0
    g27: LineSegment StartX=67 StartY=73.75 StartZ=0 EndX=64.875 EndY=70.0694 EndZ=0
    g28: LineSegment StartX=64.875 StartY=70.0694 StartZ=0 EndX=60.625 EndY=70.0694 EndZ=0
    g29: LineSegment StartX=60.625 StartY=70.0694 StartZ=0 EndX=60.524 EndY=70.2444 EndZ=0
    g30: LineSegment StartX=60.524 StartY=70.2444 StartZ=0 EndX=57.524 EndY=70.2444 EndZ=0
    g31: LineSegment StartX=57.524 StartY=70.2444 StartZ=0 EndX=57.524 EndY=77.2556 EndZ=0
    g32: LineSegment StartX=57.524 StartY=77.2556 StartZ=0 EndX=60.524 EndY=77.2556 EndZ=0
    g33: LineSegment StartX=60.524 StartY=77.2556 StartZ=0 EndX=60.625 EndY=77.4306 EndZ=0
    g34: LineSegment StartX=60.625 StartY=77.4306 StartZ=0 EndX=64.875 EndY=77.4306 EndZ=0
    g35: LineSegment StartX=64.875 StartY=77.4306 StartZ=0 EndX=67 EndY=73.75 EndZ=0
  constraints (108):
    c: Horizontal(g0)
    c: Coincident(g1,g0)
    c: Coincident(g2,g0)
    c: Coincident(g4,g3)
    c: Horizontal(g4)
    c: Coincident(g5,g4)
    c: Coincident(g6,g5)
    c: Horizontal(g6)
    c: Coincident(g7,g6)
    c: Vertical(g7)
    c: Coincident(g8,g7)
    c: Coincident(g8,g1)
    c: Angle(g0,g2) = 2.0944
    c: Coincident(g2,g3)
    c: Distance(g2) = 4.25
    c: Distance(g3) = 4.25
    c: DistanceY(g2) = 38
    c: Angle(g3,g4) = 2.0944
    c: DistanceX(g2) = 1
    c: Distance(g4) = 4.25
    c: Distance(g0) = 4.25
    c: Angle(g4,g5) = 2.0944
    c: Angle(g1,g0) = 2.0944
    c: DistanceY(g1,g1) = 0.175
    c: Horizontal(g8)
    c: DistanceX(g8,g8) = 3
    c: Coincident(g10,g9)
    c: Horizontal(g10)
    c: Coincident(g11,g10)
    c: Coincident(g15,g14)
    c: Horizontal(g15)
    c: Coincident(g16,g15)
    c: Vertical(g16)
    c: Coincident(g17,g16)
    c: Coincident(g17,g9)
    c: Horizontal(g17)
    c: Angle(g11,g10) = 2.0944
    c: Angle(g12,g11) = 2.0944
    c: Coincident(g11,g12)
    c: Angle(g13,g12) = 2.0944
    c: Coincident(g13,g14)
    c: Coincident(g12,g13)
    c: Angle(g14,g13) = 2.0944
    c: Angle(g10,g9) = 2.0944
    c: DistanceX(g14,g9) = 0
    c: DistanceX(g13,g9) = 0
    c: Distance(g10) = 4.25
    c: Distance(g11) = 4.25
    c: Distance(g13) = 4.25
    c: DistanceX(g17,g17) = 3
    c: DistanceY(g5,g4) = 0.175
    c: DistanceX(g2,g11) = 66
    c: DistanceY(g11,g2) = 0
    c: DistanceY(g15,g6) = 0
    c: Coincident(g18,g19)
    c: Horizontal(g19)
    c: Coincident(g19,g20)
    c: Coincident(g20,g21)
    c: Horizontal(g21)
    c: Coincident(g21,g22)
    c: Vertical(g22)
    c: Coincident(g22,g23)
    c: Coincident(g23,g24)
    c: Coincident(g24,g25)
    c: Horizontal(g25)
    c: Coincident(g25,g26)
    c: Coincident(g26,g18)
    c: DistanceX(g18,g2) = 0
    c: DistanceY(g2,g18) = 35.75
    c: Angle(g18,g26) = 2.0944
    c: Angle(g26,g25) = 2.0944
    c: Angle(g20,g19) = 2.0944
    c: Angle(g25,g24) = 2.0944
    c: DistanceY(g23,g24) = 0.175
    c: DistanceY(g19,g20) = 0.175
    c: Distance(g21) = 3
    c: Horizontal(g23)
    c: Coincident(g27,g28)
    c: Horizontal(g28)
    c: Coincident(g28,g29)
    c: Coincident(g29,g30)
    c: Horizontal(g30)
    c: Coincident(g30,g31)
    c: Vertical(g31)
    c: Coincident(g31,g32)
    c: Horizontal(g32)
    c: Coincident(g32,g33)
    c: Coincident(g33,g34)
    c: Horizontal(g34)
    c: Coincident(g34,g35)
    c: Coincident(g35,g27)
    c: DistanceX(g11,g27) = 0
    c: DistanceY(g18,g27) = 0
    c: Angle(g27,g28) = 2.0944
    c: Angle(g35,g27) = 2.0944
    c: Angle(g33,g34) = 2.0944
    c: DistanceX(g32,g32) = 3
    c: Angle(g28,g29) = 2.0944
    c: DistanceY(g28,g29) = 0.175
    c: DistanceY(g32,g33) = 0.175
    c: DistanceX(g30,g15) = 0
    c: Distance(g18) = 4.25
    c: Distance(g26) = 4.25
    c: Distance(g19) = 4.25
    c: Distance(g25) = 4.25
    c: Distance(g28) = 4.25
    c: Distance(g27) = 4.25
    c: Distance(g35) = 4.25
FEATURE [Part::Extrusion] Extrude003  label="m4InletTopCut"
  Base = -> Sketch003
  Dir = (0,0,-1)
  DirMode = 2
  FaceMakerClass = Part::FaceMakerBullseye
  LengthFwd = 2.5
  LengthRev = 0
  Placement = pos=(0,0,-2.75) rot=(0,0,1;0rad)
  Solid = true
  Symmetric = false
FEATURE [Part::Box] Box005  label="baseTopCut"
  AttacherType = Attacher::AttachEngine3D
  Height = 8
  Length = 51
  Placement = pos=(10.5,33.5,20) rot=(0,0,1;0rad)
  Width = 44
FEATURE [Part::Feature] Part__Feature060  label="logoTopCut"
  Placement = pos=(25,-2,35) rot=(-1,0,0;1.5708rad)
  shape: bbox 22.79 x 17.08 x 8 mm, 886 faces (baked)
FEATURE [Mesh::Feature] mintsLogo80P___90CutBase  label="mintsLogo80P - 90CutBase"
  Placement = pos=(56.35,12.9,26) rot=(0,0,1;0rad)
FEATURE [Part::Cylinder] Cylinder012
  Angle = 360
  AttacherType = Attacher::AttachEngine3D
  FirstAngle = 0
  Height = 3.15
  Placement = pos=(7.25,73.75,2) rot=(0,0,1;0rad)
  Radius = 3.6
  SecondAngle = 0
FEATURE [Part::Cylinder] Cylinder013
  Angle = 360
  AttacherType = Attacher::AttachEngine3D
  FirstAngle = 0
  Height = 3.15
  Placement = pos=(64.75,38,2) rot=(0,0,1;0rad)
  Radius = 3.6
  SecondAngle = 0
FEATURE [Part::Cylinder] Cylinder014
  Angle = 360
  AttacherType = Attacher::AttachEngine3D
  FirstAngle = 0
  Height = 3.15
  Placement = pos=(7.25,38,2) rot=(0,0,1;0rad)
  Radius = 3.6
  SecondAngle = 0
FEATURE [Part::Cylinder] Cylinder015
  Angle = 360
  AttacherType = Attacher::AttachEngine3D
  FirstAngle = 0
  Height = 3.15
  Placement = pos=(64.75,73.75,2) rot=(0,0,1;0rad)
  Radius = 3.6
  SecondAngle = 0
FEATURE [Part::MultiFuse] Fusion007  label="m4headBottomCut"
  Placement = pos=(0,0,-2) rot=(0,0,1;0rad)
  Shapes = -> [Cylinder015,Cylinder012,Cylinder013,Cylinder014]
FEATURE [Sketcher::SketchObject] Sketch004
  FullyConstrained = true
  Placement = pos=(0,0,0) rot=(1,0,0;1.5708rad)
  sketch-geometry (46):
    g0: LineSegment StartX=11.75 StartY=19.5 StartZ=0 EndX=21.5 EndY=19.5 EndZ=0
    g1: LineSegment StartX=21.5 StartY=19.5 StartZ=0 EndX=23.75 EndY=22 EndZ=0
    g2: LineSegment StartX=23.75 StartY=22 StartZ=0 EndX=23.75 EndY=25 EndZ=0
    g3: LineSegment StartX=23.75 StartY=25 StartZ=0 EndX=9.5 EndY=25 EndZ=0
    g4: LineSegment StartX=9.5 StartY=25 StartZ=0 EndX=9.5 EndY=22 EndZ=0
    g5: LineSegment StartX=40 StartY=24.5 StartZ=0 EndX=40 EndY=22 EndZ=0
    g6: LineSegment StartX=40 StartY=22 StartZ=0 EndX=42.5 EndY=19.5 EndZ=0
    g7: LineSegment StartX=42.5 StartY=19.5 StartZ=0 EndX=48.7 EndY=19.5 EndZ=0
    g8: LineSegment StartX=48.7 StartY=19.5 StartZ=0 EndX=51.2 EndY=22 EndZ=0
    g9: LineSegment StartX=51.2 StartY=22 StartZ=0 EndX=51.2 EndY=24.5 EndZ=0
    g10: LineSegment StartX=51.2 StartY=24.5 StartZ=0 EndX=40 EndY=24.5 EndZ=0
    g11: LineSegment StartX=52.45 StartY=24.5 StartZ=0 EndX=52.45 EndY=22 EndZ=0
    g12: LineSegment StartX=52.45 StartY=22 StartZ=0 EndX=54.95 EndY=19.5 EndZ=0
    g13: LineSegment StartX=54.95 StartY=19.5 StartZ=0 EndX=61.15 EndY=19.5 EndZ=0
    g14: LineSegment StartX=61.15 StartY=19.5 StartZ=0 EndX=63.65 EndY=22 EndZ=0
    g15: LineSegment StartX=63.65 StartY=22 StartZ=0 EndX=63.65 EndY=24.5 EndZ=0
    g16: LineSegment StartX=63.65 StartY=24.5 StartZ=0 EndX=52.45 EndY=24.5 EndZ=0
    g17: LineSegment StartX=9.5 StartY=22 StartZ=0 EndX=11.75 EndY=19.5 EndZ=0
    g18: ArcOfCircle CenterX=12.3 CenterY=15.45 CenterZ=0 NormalX=0 NormalY=0 NormalZ=1 AngleXU=0 Radius=1 StartAngle=1.5708 EndAngle=3.14159
    g19: LineSegment StartX=11.3 StartY=15.45 StartZ=0 EndX=11.3 EndY=14.2 EndZ=0
    g20: LineSegment StartX=12.3 StartY=16.45 StartZ=0 EndX=16.8 EndY=16.45 EndZ=0
    g21: ArcOfCircle CenterX=16.8 CenterY=15.45 CenterZ=0 NormalX=0 NormalY=0 NormalZ=1 AngleXU=0 Radius=1 StartAngle=3e-16 EndAngle=1.5708
    g22: ArcOfCircle CenterX=16.8 CenterY=14.2 CenterZ=0 NormalX=0 NormalY=0 NormalZ=1 AngleXU=0 Radius=1 StartAngle=4.71239 EndAngle=6.28319
    g23: ArcOfCircle CenterX=12.3 CenterY=14.2 CenterZ=0 NormalX=0 NormalY=0 NormalZ=1 AngleXU=0 Radius=1 StartAngle=3.14159 EndAngle=4.71239
    g24: LineSegment StartX=12.3 StartY=13.2 StartZ=0 EndX=16.8 EndY=13.2 EndZ=0
    g25: LineSegment StartX=17.8 StartY=15.45 StartZ=0 EndX=17.8 EndY=14.2 EndZ=0
    g26: Circle CenterX=18.9 CenterY=16.475 CenterZ=0 NormalX=0 NormalY=0 NormalZ=1 AngleXU=0 Radius=0.5
    g27: Circle CenterX=21.09 CenterY=16.475 CenterZ=0 NormalX=0 NormalY=0 NormalZ=1 AngleXU=0 Radius=0.5
    g28: Circle CenterX=23.28 CenterY=16.475 CenterZ=0 NormalX=0 NormalY=0 NormalZ=1 AngleXU=0 Radius=0.5
    g29: Circle CenterX=25.47 CenterY=16.475 CenterZ=0 NormalX=0 NormalY=0 NormalZ=1 AngleXU=0 Radius=0.5
    g30: LineSegment StartX=44.8 StartY=16.45 StartZ=0 EndX=49.3 EndY=16.45 EndZ=0
    g31: LineSegment StartX=50.3 StartY=15.45 StartZ=0 EndX=50.3 EndY=14.2 EndZ=0
    g32: LineSegment StartX=49.3 StartY=13.2 StartZ=0 EndX=44.8 EndY=13.2 EndZ=0
    g33: LineSegment StartX=43.8 StartY=15.45 StartZ=0 EndX=43.8 EndY=14.2 EndZ=0
    g34: ArcOfCircle CenterX=44.8 CenterY=15.45 CenterZ=0 NormalX=0 NormalY=0 NormalZ=1 AngleXU=0 Radius=1 StartAngle=1.5708 EndAngle=3.14159
    g35: ArcOfCircle CenterX=49.3 CenterY=15.45 CenterZ=0 NormalX=0 NormalY=0 NormalZ=1 AngleXU=0 Radius=1 StartAngle=3e-16 EndAngle=1.5708
    g36: ArcOfCircle CenterX=49.3 CenterY=14.2 CenterZ=0 NormalX=0 NormalY=0 NormalZ=1 AngleXU=0 Radius=1 StartAngle=4.71239 EndAngle=6.28319
    g37: ArcOfCircle CenterX=44.8 CenterY=14.2 CenterZ=0 NormalX=0 NormalY=0 NormalZ=1 AngleXU=0 Radius=1 StartAngle=3.14159 EndAngle=4.71239
    g38: LineSegment StartX=52.25 StartY=15.58 StartZ=0 EndX=52.25 EndY=14.58 EndZ=0
    g39: LineSegment StartX=53.5 StartY=16.83 StartZ=0 EndX=60.5 EndY=16.83 EndZ=0
    g40: LineSegment StartX=53.5 StartY=13.33 StartZ=0 EndX=60.5 EndY=13.33 EndZ=0
    g41: LineSegment StartX=61.75 StartY=15.58 StartZ=0 EndX=61.75 EndY=14.58 EndZ=0
    g42: ArcOfCircle CenterX=53.5 CenterY=15.58 CenterZ=0 NormalX=0 NormalY=0 NormalZ=1 AngleXU=0 Radius=1.25 StartAngle=1.5708 EndAngle=3.14159
    g43: ArcOfCircle CenterX=60.5 CenterY=15.58 CenterZ=0 NormalX=0 NormalY=0 NormalZ=1 AngleXU=0 Radius=1.25 StartAngle=2e-16 EndAngle=1.5708
    g44: ArcOfCircle CenterX=60.5 CenterY=14.58 CenterZ=0 NormalX=0 NormalY=0 NormalZ=1 AngleXU=0 Radius=1.25 StartAngle=4.7124 EndAngle=6.28319
    g45: ArcOfCircle CenterX=53.5 CenterY=14.58 CenterZ=0 NormalX=0 NormalY=0 NormalZ=1 AngleXU=0 Radius=1.25 StartAngle=3.14159 EndAngle=4.71239
  constraints (150):
    c: Horizontal(g0)
    c: Coincident(g0,g1)
    c: Coincident(g1,g2)
    c: Coincident(g2,g3)
    c: Horizontal(g3)
    c: Coincident(g3,g4)
    c: Vertical(g4)
    c: Coincident(g5,g6)
    c: Coincident(g6,g7)
    c: Horizontal(g7)
    c: Coincident(g7,g8)
    c: Coincident(g8,g9)
    c: Vertical(g9)
    c: Coincident(g9,g10)
    c: Coincident(g10,g5)
    c: Coincident(g11,g12)
    c: Coincident(g12,g13)
    c: Horizontal(g13)
    c: Coincident(g13,g14)
    c: Coincident(g14,g15)
    c: Vertical(g15)
    c: Coincident(g15,g16)
    c: Coincident(g16,g11)
    c: Horizontal(g16)
    c: Coincident(g17,g4)
    c: Coincident(g0,g17)
    c: DistanceX(g3) = 9.5
    c: DistanceX(g3,g3) = 14.25
    c: Vertical(g2)
    c: DistanceY(g3) = 25
    c: DistanceY(g4) = 22
    c: DistanceY(g4,g1) = 0
    c: DistanceX(g4,g0) = 2.25
    c: DistanceX(g0,g1) = 2.25
    c: Horizontal(g10)
    c: Vertical(g5)
    c: Vertical(g11)
    c: DistanceX(g5) = 40
    c: DistanceX(g5,g9) = 11.2
    c: DistanceY(g11,g9) = 0
    c: DistanceY(g5,g5) = 2.5
    c: DistanceY(g8,g5) = 0
    c: DistanceY(g11,g8) = 0
    c: DistanceY(g14,g11) = 0
    c: DistanceY(g6,g5) = 2.5
    c: DistanceX(g5,g6) = 2.5
    c: DistanceX(g7,g8) = 2.5
    c: DistanceX(g9,g11) = 1.25
    c: DistanceY(g12,g7) = 0
    c: DistanceX(g11,g12) = 2.5
    c: DistanceX(g13,g14) = 2.5
    c: DistanceX(g11,g15) = 11.2
    c: DistanceY(g0,g4) = 2.5
    c: DistanceY(g5) = 24.5
    c: Coincident(g19,g18)
    c: Vertical(g19)
    c: Horizontal(g20)
    c: Coincident(g21,g20)
    c: Coincident(g23,g19)
    c: Coincident(g24,g23)
    c: Coincident(g24,g22)
    c: Horizontal(g24)
    c: Coincident(g25,g21)
    c: Coincident(g25,g22)
    c: Vertical(g25)
    c: Coincident(g18,g20)
    c: Radius(g18) = 1
    c: Angle(g18) = 1.5708
    c: Angle(g21) = 1.5708
    c: Angle(g22) = 1.5708
    c: Angle(g23) = 1.5708
    c: DistanceX(g23) = 12.3
    c: DistanceY(g23) = 13.2
    c: DistanceX(g19) = 11.3
    c: DistanceY(g23,g19) = 0
    c: DistanceY(g18,g18) = 0
    c: DistanceX(g21,g20) = 0
    c: Radius(g21) = 1
    c: Radius(g22) = 1
    c: DistanceX(g22,g22) = 0
    c: DistanceX(g18,g20) = 4.5
    c: DistanceX(g26) = 18.9
    c: Radius(g26) = 0.5
    c: DistanceY(g26) = 16.475
    c: DistanceX(g26,g27) = 2.19
    c: DistanceY(g26,g27) = 0
    c: DistanceY(g28,g27) = 0
    c: DistanceY(g29,g28) = 0
    c: DistanceX(g27,g28) = 2.19
    c: Radius(g27) = 0.5
    c: Radius(g28) = 0.5
    c: Radius(g29) = 0.5
    c: DistanceX(g28,g29) = 2.19
    c: DistanceY(g23,g18) = 1.25
    c: Horizontal(g30)
    c: Vertical(g31)
    c: Vertical(g33)
    c: Coincident(g33,g34)
    c: Coincident(g33,g37)
    c: Coincident(g32,g37)
    c: Coincident(g32,g36)
    c: Coincident(g31,g36)
    c: Coincident(g31,g35)
    c: Coincident(g30,g35)
    c: Coincident(g30,g34)
    c: Angle(g34) = 1.5708
    c: Angle(g35) = 1.5708
    c: Angle(g37) = 1.5708
    c: Angle(g36) = 1.5708
    c: DistanceY(g18,g34) = 0
    c: DistanceY(g34,g33) = 0
    c: Radius(g34) = 1
    c: DistanceY(g33,g37) = 0
    c: Radius(g37) = 1
    c: Radius(g36) = 1
    c: Radius(g35) = 1
    c: DistanceY(g33,g23) = 0
    c: DistanceY(g31,g36) = 0
    c: Horizontal(g32)
    c: DistanceX(g35,g30) = 0
    c: DistanceX(g32,g32) = 4.5
    c: Vertical(g38)
    c: Horizontal(g39)
    c: Horizontal(g40)
    c: Vertical(g41)
    c: Coincident(g42,g38)
    c: Coincident(g42,g39)
    c: Coincident(g43,g39)
    c: Coincident(g45,g38)
    c: Coincident(g45,g40)
    c: Coincident(g40,g44)
    c: Coincident(g41,g44)
    c: Coincident(g41,g43)
    c: DistanceX(g42) = 53.5
    c: DistanceY(g42) = 15.58
    c: DistanceX(g42,g45) = 0
    c: DistanceY(g45,g42) = 1
    c: Radius(g42) = 1.25
    c: Radius(g44) = 1.25
    c: Radius(g43) = 1.25
    c: DistanceX(g45,g40) = 0
    c: DistanceX(g42,g39) = 0
    c: DistanceY(g42,g43) = 0
    c: DistanceY(g44,g45) = 0
    c: DistanceY(g45,g38) = 0
    c: DistanceX(g42,g43) = 7
    c: DistanceX(g18,g34) = 32.5
    c: DistanceY(g41,g44) = 0
    c: DistanceY(g43,g41) = 0
    c: Angle(g42) = 1.5708
FEATURE [Part::Extrusion] Extrude004  label="lightBottomCut"
  Base = -> Sketch004
  Dir = (0,-1,2e-16)
  DirMode = 2
  FaceMakerClass = Part::FaceMakerBullseye
  LengthFwd = 2
  LengthRev = 0
  Placement = pos=(0,2,0) rot=(0,0,1;0rad)
  Solid = true
  Symmetric = false
FEATURE [Sketcher::SketchObject] Sketch007
  FullyConstrained = true
  sketch-geometry (48):
    g0: LineSegment StartX=4 StartY=77 StartZ=0 EndX=6 EndY=77 EndZ=0
    g1: LineSegment StartX=6 StartY=77 StartZ=0 EndX=-3.99999 EndY=59.6795 EndZ=0
    g2: LineSegment StartX=-3.99999 StartY=59.6795 StartZ=0 EndX=-5.99999 EndY=59.6795 EndZ=0
    g3: LineSegment StartX=-5.99999 StartY=59.6795 StartZ=0 EndX=4 EndY=77 EndZ=0
    g4: LineSegment StartX=-5.99999 StartY=52.6795 StartZ=0 EndX=-3.99999 EndY=52.6795 EndZ=0
    g5: LineSegment StartX=-5.99999 StartY=52.6795 StartZ=0 EndX=4 EndY=70 EndZ=0
    g6: LineSegment StartX=4 StartY=70 StartZ=0 EndX=6 EndY=70 EndZ=0
    g7: LineSegment StartX=6 StartY=70 StartZ=0 EndX=-3.99999 EndY=52.6795 EndZ=0
    g8: LineSegment StartX=-3.99999 StartY=45.6795 StartZ=0 EndX=-5.99999 EndY=45.6795 EndZ=0
    g9: LineSegment StartX=-5.99999 StartY=45.6795 StartZ=0 EndX=4 EndY=63 EndZ=0
    g10: LineSegment StartX=4 StartY=63 StartZ=0 EndX=6 EndY=63 EndZ=0
    g11: LineSegment StartX=6 StartY=63 StartZ=0 EndX=-3.99999 EndY=45.6795 EndZ=0
    g12: LineSegment StartX=4 StartY=56 StartZ=0 EndX=6 EndY=56 EndZ=0
    g13: LineSegment StartX=6 StartY=56 StartZ=0 EndX=-3.99999 EndY=38.6795 EndZ=0
    g14: LineSegment StartX=-3.99999 StartY=38.6795 StartZ=0 EndX=-5.99999 EndY=38.6795 EndZ=0
    g15: LineSegment StartX=-5.99999 StartY=38.6795 StartZ=0 EndX=4 EndY=56 EndZ=0
    g16: LineSegment StartX=4 StartY=49 StartZ=0 EndX=6 EndY=49 EndZ=0
    g17: LineSegment StartX=6 StartY=49 StartZ=0 EndX=-3.99999 EndY=31.6795 EndZ=0
    g18: LineSegment StartX=-3.99999 StartY=31.6795 StartZ=0 EndX=-5.99999 EndY=31.6795 EndZ=0
    g19: LineSegment StartX=-5.99999 StartY=31.6795 StartZ=0 EndX=4 EndY=49 EndZ=0
    g20: LineSegment StartX=4 StartY=42 StartZ=0 EndX=6 EndY=42 EndZ=0
    g21: LineSegment StartX=6 StartY=42 StartZ=0 EndX=-3.99999 EndY=24.6795 EndZ=0
    g22: LineSegment StartX=-3.99999 StartY=24.6795 StartZ=0 EndX=-5.99999 EndY=24.6795 EndZ=0
    g23: LineSegment StartX=-5.99999 StartY=24.6795 StartZ=0 EndX=4 EndY=42 EndZ=0
    g24: LineSegment StartX=68 StartY=77 StartZ=0 EndX=66 EndY=77 EndZ=0
    g25: LineSegment StartX=66 StartY=77 StartZ=0 EndX=76 EndY=59.6795 EndZ=0
    g26: LineSegment StartX=76 StartY=59.6795 StartZ=0 EndX=78 EndY=59.6795 EndZ=0
    g27: LineSegment StartX=78 StartY=59.6795 StartZ=0 EndX=68 EndY=77 EndZ=0
    g28: LineSegment StartX=66 StartY=70 StartZ=0 EndX=68 EndY=70 EndZ=0
    g29: LineSegment StartX=68 StartY=70 StartZ=0 EndX=78 EndY=52.6795 EndZ=0
    g30: LineSegment StartX=78 StartY=52.6795 StartZ=0 EndX=76 EndY=52.6795 EndZ=0
    g31: LineSegment StartX=76 StartY=52.6795 StartZ=0 EndX=66 EndY=70 EndZ=0
    g32: LineSegment StartX=66 StartY=63 StartZ=0 EndX=68 EndY=63 EndZ=0
    g33: LineSegment StartX=68 StartY=63 StartZ=0 EndX=78 EndY=45.6795 EndZ=0
    g34: LineSegment StartX=78 StartY=45.6795 StartZ=0 EndX=76 EndY=45.6795 EndZ=0
    g35: LineSegment StartX=76 StartY=45.6795 StartZ=0 EndX=66 EndY=63 EndZ=0
    g36: LineSegment StartX=66 StartY=56 StartZ=0 EndX=68 EndY=56 EndZ=0
    g37: LineSegment StartX=68 StartY=56 StartZ=0 EndX=78 EndY=38.6795 EndZ=0
    g38: LineSegment StartX=78 StartY=38.6795 StartZ=0 EndX=76 EndY=38.6795 EndZ=0
    g39: LineSegment StartX=76 StartY=38.6795 StartZ=0 EndX=66 EndY=56 EndZ=0
    g40: LineSegment StartX=66 StartY=49 StartZ=0 EndX=68 EndY=49 EndZ=0
    g41: LineSegment StartX=68 StartY=49 StartZ=0 EndX=78 EndY=31.6795 EndZ=0
    g42: LineSegment StartX=78 StartY=31.6795 StartZ=0 EndX=76 EndY=31.6795 EndZ=0
    g43: LineSegment StartX=76 StartY=31.6795 StartZ=0 EndX=66 EndY=49 EndZ=0
    g44: LineSegment StartX=66 StartY=42 StartZ=0 EndX=68 EndY=42 EndZ=0
    g45: LineSegment StartX=68 StartY=42 StartZ=0 EndX=78 EndY=24.6795 EndZ=0
    g46: LineSegment StartX=78 StartY=24.6795 StartZ=0 EndX=76 EndY=24.6795 EndZ=0
    g47: LineSegment StartX=76 StartY=24.6795 StartZ=0 EndX=66 EndY=42 EndZ=0
  constraints (144):
    c: Coincident(g3,g0)
    c: DistanceX(g2,g2) = 2
    c: DistanceX(g0,g0) = 2
    c: Angle(g1) = -2.0944
    c: Distance(g3) = 20
    c: Coincident(g2,g3)
    c: DistanceX(g0) = 4
    c: DistanceY(g0) = 77
    c: Coincident(g4,g5)
    c: Coincident(g6,g7)
    c: Coincident(g7,g4)
    c: Horizontal(g6)
    c: DistanceX(g5,g0) = 0
    c: DistanceY(g5,g0) = 7
    c: DistanceX(g2,g4) = 0
    c: DistanceX(g1,g4) = 0
    c: DistanceY(g4,g2) = 7
    c: Horizontal(g4)
    c: Angle(g5) = 1.0472
    c: Horizontal(g8)
    c: Coincident(g9,g8)
    c: Horizontal(g10)
    c: Coincident(g11,g8)
    c: Coincident(g9,g10)
    c: Coincident(g10,g11)
    c: DistanceX(g5,g9) = 0
    c: DistanceX(g10,g6) = 0
    c: DistanceY(g9,g5) = 7
    c: DistanceY(g8,g4) = 7
    c: DistanceX(g8,g4) = 0
    c: DistanceX(g4,g8) = 0
    c: Horizontal(g12)
    c: Coincident(g13,g12)
    c: Horizontal(g14)
    c: Coincident(g15,g12)
    c: Coincident(g1,g2)
    c: Horizontal(g2)
    c: DistanceX(g12,g12) = 2
    c: DistanceX(g9,g12) = 0
    c: DistanceY(g12,g9) = 7
    c: DistanceY(g14,g8) = 7
    c: Coincident(g14,g13)
    c: Coincident(g14,g15)
    c: DistanceX(g14,g8) = 0
    c: DistanceX(g8,g13) = 0
    c: Horizontal(g16)
    c: Coincident(g17,g16)
    c: Horizontal(g18)
    c: Coincident(g19,g16)
    c: DistanceX(g16,g16) = 2
    c: DistanceY(g16,g12) = 7
    c: DistanceX(g12,g16) = 0
    c: DistanceX(g18,g14) = 0
    c: Coincident(g18,g19)
    c: Coincident(g17,g18)
    c: DistanceY(g18,g14) = 7
    c: DistanceX(g18,g18) = 2
    c: Horizontal(g20)
    c: Coincident(g20,g21)
    c: Coincident(g21,g22)
    c: Coincident(g22,g23)
    c: Coincident(g23,g20)
    c: DistanceX(g16,g20) = 0
    c: DistanceY(g20,g16) = 7
    c: DistanceY(g22,g18) = 7
    c: DistanceX(g22,g18) = 0
    c: Horizontal(g22)
    c: DistanceX(g22,g22) = 2
    c: DistanceX(g20,g20) = 2
    c: Horizontal(g24)
    c: Coincident(g25,g24)
    c: Coincident(g26,g25)
    c: Horizontal(g26)
    c: Coincident(g27,g24)
    c: DistanceX(g24,g24) = 2
    c: DistanceX(g0,g24) = 64
    c: DistanceY(g24,g0) = 0
    c: Distance(g25) = 20
    c: Coincident(g26,g27)
    c: Angle(g27) = 2.0944
    c: DistanceX(g26,g26) = 2
    c: Horizontal(g28)
    c: Coincident(g29,g28)
    c: Coincident(g30,g29)
    c: Coincident(g31,g28)
    c: Coincident(g33,g32)
    c: Coincident(g34,g33)
    c: Coincident(g35,g32)
    c: Coincident(g37,g36)
    c: Coincident(g38,g37)
    c: Coincident(g39,g36)
    c: DistanceY(g28,g6) = 0
    c: DistanceY(g32,g9) = 0
    c: DistanceY(g36,g12) = 0
    c: DistanceX(g24,g28) = 0
    c: DistanceX(g32,g28) = 0
    c: DistanceX(g36,g32) = 0
    c: Horizontal(g36)
    c: Horizontal(g32)
    c: DistanceX(g32,g32) = 2
    c: DistanceX(g36,g36) = 2
    c: Horizontal(g30)
    c: Horizontal(g34)
    c: Horizontal(g38)
    c: Coincident(g34,g35)
    c: Coincident(g30,g31)
    c: DistanceX(g25,g30) = 0
    c: DistanceX(g30,g34) = 0
    c: DistanceX(g34,g34) = 2
    c: DistanceX(g30,g30) = 2
    c: Coincident(g38,g39)
    c: DistanceX(g38,g38) = 2
    c: DistanceX(g34,g38) = 0
    c: Horizontal(g40)
    c: Coincident(g41,g40)
    c: Horizontal(g42)
    c: Coincident(g43,g40)
    c: DistanceY(g40,g16) = 0
    c: Horizontal(g44)
    c: Coincident(g45,g44)
    c: Coincident(g46,g45)
    c: Horizontal(g46)
    c: Coincident(g47,g44)
    c: DistanceY(g20,g44) = 0
    c: DistanceX(g44,g40) = 0
    c: DistanceX(g40,g36) = 0
    c: DistanceX(g44,g44) = 2
    c: DistanceX(g40,g40) = 2
    c: DistanceX(g46,g46) = 2
    c: DistanceX(g42,g42) = 2
    c: Coincident(g42,g43)
    c: Coincident(g41,g42)
    c: Coincident(g46,g47)
    c: DistanceX(g42,g38) = 0
    c: DistanceX(g46,g42) = 0
    c: DistanceY(g46,g42) = 7
    c: DistanceY(g42,g38) = 7
    c: DistanceY(g38,g34) = 7
    c: DistanceY(g34,g30) = 7
    c: DistanceY(g30,g25) = 7
    c: DistanceX(g28,g28) = 2
    c: Coincident(g0,g1)
    c: DistanceX(g6,g6) = 2
    c: Coincident(g5,g6)
FEATURE [Part::Extrusion] Extrude007  label="ventsBottomCut"
  Base = -> Sketch007
  Dir = (0,0,1)
  DirMode = 2
  FaceMakerClass = Part::FaceMakerBullseye
  LengthFwd = 20
  LengthRev = 0
  Placement = pos=(0,0,5) rot=(0,0,1;0rad)
  Solid = true
  Symmetric = false
FEATURE [Part::Cylinder] Cylinder016
  Angle = 360
  AttacherType = Attacher::AttachEngine3D
  FirstAngle = 0
  Height = 14
  Placement = pos=(7.25,73.75,2) rot=(0,0,1;0rad)
  Radius = 2.1
  SecondAngle = 0
FEATURE [Part::Cylinder] Cylinder017
  Angle = 360
  AttacherType = Attacher::AttachEngine3D
  FirstAngle = 0
  Height = 14
  Placement = pos=(64.75,38,2) rot=(0,0,1;0rad)
  Radius = 2.1
  SecondAngle = 0
FEATURE [Part::Cylinder] Cylinder018
  Angle = 360
  AttacherType = Attacher::AttachEngine3D
  FirstAngle = 0
  Height = 14
  Placement = pos=(7.25,38,2) rot=(0,0,1;0rad)
  Radius = 2.1
  SecondAngle = 0
FEATURE [Part::Cylinder] Cylinder019
  Angle = 360
  AttacherType = Attacher::AttachEngine3D
  FirstAngle = 0
  Height = 14
  Placement = pos=(64.75,73.75,2) rot=(0,0,1;0rad)
  Radius = 2.1
  SecondAngle = 0
FEATURE [Part::MultiFuse] Fusion009  label="basesM4TopCut"
  Placement = pos=(0,0,12.25) rot=(0,0,1;0rad)
  Shapes = -> [Cylinder019,Cylinder016,Cylinder017,Cylinder018]
FEATURE [Sketcher::SketchObject] Sketch008
  FullyConstrained = true
  MapMode = 2
  Placement = pos=(0,0,12.25) rot=(0,0,1;0rad)
  Support = -> [Fusion009]
  sketch-geometry (10):
    g0: LineSegment StartX=2.5 StartY=78.5 StartZ=0 EndX=2.5 EndY=2.5 EndZ=0
    g1: LineSegment StartX=2.5 StartY=2.5 StartZ=0 EndX=35 EndY=2.5 EndZ=0
    g2: LineSegment StartX=69.5 StartY=21.25 StartZ=0 EndX=69.5 EndY=78.5 EndZ=0
    g3: LineSegment StartX=2.5 StartY=78.5 StartZ=0 EndX=69.5 EndY=78.5 EndZ=0
    g4: LineSegment StartX=35 StartY=2.5 StartZ=0 EndX=35 EndY=3.5 EndZ=0
    g5: LineSegment StartX=35 StartY=3.5 StartZ=0 EndX=3.5 EndY=3.5 EndZ=0
    g6: LineSegment StartX=3.5 StartY=3.5 StartZ=0 EndX=3.5 EndY=77.5 EndZ=0
    g7: LineSegment StartX=3.5 StartY=77.5 StartZ=0 EndX=68.5 EndY=77.5 EndZ=0
    g8: LineSegment StartX=68.5 StartY=77.5 StartZ=0 EndX=68.5 EndY=21.25 EndZ=0
    g9: LineSegment StartX=68.5 StartY=21.25 StartZ=0 EndX=69.5 EndY=21.25 EndZ=0
  constraints (30):
    c: Vertical(g0)
    c: Horizontal(g1)
    c: Vertical(g2)
    c: Coincident(g3,g2)
    c: DistanceX(g-1,g0) = 2.5
    c: DistanceY(g0) = 2.5
    c: Coincident(g1,g0)
    c: Coincident(g0,g3)
    c: Coincident(g4,g1)
    c: Vertical(g4)
    c: Horizontal(g5)
    c: Coincident(g6,g5)
    c: Vertical(g6)
    c: Horizontal(g7)
    c: Coincident(g8,g7)
    c: Vertical(g8)
    c: Coincident(g9,g8)
    c: Coincident(g9,g2)
    c: DistanceX(g5) = 3.5
    c: DistanceY(g-1,g5) = 3.5
    c: DistanceX(g0,g1) = 32.5
    c: Coincident(g5,g4)
    c: Coincident(g6,g7)
    c: DistanceY(g0,g0) = 76
    c: DistanceY(g6,g0) = 1
    c: DistanceX(g7,g2) = 1
    c: DistanceX(g0,g2) = 67
    c: Horizontal(g9)
    c: DistanceY(g8,g7) = 56.25
    c: Horizontal(g3)
FEATURE [Part::Extrusion] Extrude008  label="topAlineIn"
  Base = -> Sketch008
  Dir = (0,0,1)
  DirMode = 2
  FaceMakerClass = Part::FaceMakerBullseye
  LengthFwd = 1.5
  LengthRev = 0
  Placement = pos=(0,0,15) rot=(0,0,1;0rad)
  Solid = true
  Symmetric = false
FEATURE [Part::Cut] Cut002  label="bottom004"
  Base = -> Cut
  Tool = -> Extrude007
FEATURE [Sketcher::SketchObject] Sketch009
  FullyConstrained = true
  MapMode = 4
  Placement = pos=(0,0,0) rot=(0.57735,0.57735,0.57735;2.0944rad)
  sketch-geometry (1):
    g0: Circle CenterX=79 CenterY=2 CenterZ=0 NormalX=0 NormalY=0 NormalZ=1 AngleXU=0 Radius=2
  constraints (3):
    c: DistanceX(g0) = 79
    c: DistanceY(g0) = 2
    c: Radius(g0) = 2
FEATURE [Part::Extrusion] Extrude009  label="bottomInTagHoldIn"
  Base = -> Sketch009
  Dir = (1,0,0)
  DirMode = 2
  FaceMakerClass = Part::FaceMakerBullseye
  LengthFwd = 68
  LengthRev = 0
  Placement = pos=(2,0,0) rot=(0,0,1;0rad)
  Solid = true
  Symmetric = false
FEATURE [Sketcher::SketchObject] Sketch011
  FullyConstrained = true
  Placement = pos=(0,0,0) rot=(0.57735,0.57735,0.57735;2.0944rad)
  sketch-geometry (2):
    g0: Circle CenterX=79 CenterY=2 CenterZ=0 NormalX=0 NormalY=0 NormalZ=1 AngleXU=0 Radius=3.5
    g1: Circle CenterX=79 CenterY=2 CenterZ=0 NormalX=0 NormalY=0 NormalZ=1 AngleXU=0 Radius=2
  constraints (5):
    c: Radius(g0) = 3.5
    c: Radius(g1) = 2
    c: Coincident(g0,g1)
    c: DistanceX(g0) = 79
    c: DistanceY(g0) = 2
FEATURE [Part::Extrusion] Extrude011  label="tagBottomCut001"
  Base = -> Sketch011
  Dir = (1,0,0)
  DirMode = 2
  FaceMakerClass = Part::FaceMakerBullseye
  LengthFwd = 10
  LengthRev = 0
  Placement = pos=(31,0,0) rot=(0,0,1;0rad)
  Solid = true
  Symmetric = false
FEATURE [Mesh::Feature] pisugar3_shell_xl
  Placement = pos=(-2.51,33.56,0.45) rot=(-1,0,0;4.71239rad)
FEATURE [Part::MultiFuse] Fusion012  label="bottomIn"
  Shapes = -> [Extrude009,Cut002,Fillet004,Fillet003,Fusion]
FEATURE [Part::MultiFuse] Fusion014  label="topBasesIn"
  Placement = pos=(0,0,18.25) rot=(0,0,1;0rad)
  Shapes = -> [Cylinder008,Cylinder009,Cylinder010,Cylinder011]
FEATURE [Part::MultiFuse] Fusion015  label="topIn"
  Shapes = -> [Fusion014,Extrude008,Fillet005]
FEATURE [Part::MultiFuse] Fusion016  label="topCuts"
  Shapes = -> [Fusion009,Part__Feature060,Box005,Extrude003]
FEATURE [Part::Cut] Cut004  label="top002"
  Base = -> Fusion015
  Tool = -> Fusion016
FEATURE [Sketcher::SketchObject] Sketch012
  FullyConstrained = true
  Placement = pos=(0,0,0) rot=(0.57735,0.57735,0.57735;2.0944rad)
  sketch-geometry (4):
    g0: LineSegment StartX=8 StartY=23 StartZ=0 EndX=26 EndY=23 EndZ=0
    g1: LineSegment StartX=26 StartY=23 StartZ=0 EndX=26 EndY=20 EndZ=0
    g2: LineSegment StartX=26 StartY=20 StartZ=0 EndX=8 EndY=20 EndZ=0
    g3: LineSegment StartX=8 StartY=20 StartZ=0 EndX=8 EndY=23 EndZ=0
  constraints (12):
    c: Coincident(g0,g1)
    c: Coincident(g1,g2)
    c: Coincident(g2,g3)
    c: Coincident(g3,g0)
    c: Horizontal(g0)
    c: Horizontal(g2)
    c: Vertical(g1)
    c: Vertical(g3)
    c: DistanceX(g2) = 8
    c: DistanceX(g2,g0) = 18
    c: DistanceY(g2) = 20
    c: DistanceY(g2,g0) = 3
FEATURE [Part::Extrusion] Extrude012  label="leftInCut"
  Base = -> Sketch012
  Dir = (1,0,0)
  DirMode = 2
  FaceMakerClass = Part::FaceMakerBullseye
  LengthFwd = 2
  LengthRev = 0
  Placement = pos=(70,0,0) rot=(0,0,1;0rad)
  Solid = true
  Symmetric = false
FEATURE [Sketcher::SketchObject] Sketch013
  FullyConstrained = true
  MapMode = 4
  Placement = pos=(70,0,0) rot=(0.57735,0.57735,0.57735;2.0944rad)
  Support = -> [Extrude012]
  sketch-geometry (4):
    g0: LineSegment StartX=26 StartY=19.9 StartZ=0 EndX=12 EndY=19.9 EndZ=0
    g1: LineSegment StartX=12 StartY=19.9 StartZ=0 EndX=12 EndY=22.9 EndZ=0
    g2: LineSegment StartX=12 StartY=22.9 StartZ=0 EndX=26 EndY=22.9 EndZ=0
    g3: LineSegment StartX=26 StartY=22.9 StartZ=0 EndX=26 EndY=19.9 EndZ=0
  constraints (12):
    c: Coincident(g0,g1)
    c: Coincident(g1,g2)
    c: Coincident(g2,g3)
    c: Coincident(g3,g0)
    c: Horizontal(g0)
    c: Horizontal(g2)
    c: Vertical(g1)
    c: Vertical(g3)
    c: DistanceX(g0,g0) = 14
    c: DistanceX(g1) = 12
    c: DistanceY(g1) = 22.9
    c: DistanceY(g1,g1) = 3
FEATURE [Part::Extrusion] Extrude013  label="sdCut"
  Base = -> Sketch013
  Dir = (1,0,0)
  DirMode = 2
  FaceMakerClass = Part::FaceMakerBullseye
  LengthFwd = 2
  LengthRev = 0
  Placement = pos=(-70,0,0) rot=(0,0,1;0rad)
  Solid = true
  Symmetric = false
FEATURE [Part::MultiFuse] Fusion017  label="bottomCutsHor"
  Shapes = -> [Extrude013,Extrude012]
FEATURE [Mesh::Feature] pisugar3_button
  Placement = pos=(-35.433,33.594,-1.06e-14) rot=(-1,0,0;4.71239rad)
FEATURE [Mesh::Feature] pisugar3_button001
  Placement = pos=(-2.93,33.59,0) rot=(-1,0,0;4.71239rad)
FEATURE [Sketcher::SketchObject] Sketch014
  FullyConstrained = true
  Placement = pos=(0,0,0) rot=(1,0,0;1.5708rad)
  sketch-geometry (8):
    g0: ArcOfCircle CenterX=12.4 CenterY=15.35 CenterZ=0 NormalX=0 NormalY=0 NormalZ=1 AngleXU=0 Radius=0.9 StartAngle=1.5708 EndAngle=3.14159
    g1: ArcOfCircle CenterX=16.7 CenterY=15.35 CenterZ=0 NormalX=0 NormalY=0 NormalZ=1 AngleXU=0 Radius=0.9 StartAngle=9e-16 EndAngle=1.5708
    g2: ArcOfCircle CenterX=16.7 CenterY=14.3 CenterZ=0 NormalX=0 NormalY=0 NormalZ=1 AngleXU=0 Radius=0.9 StartAngle=4.71239 EndAngle=6.28319
    g3: ArcOfCircle CenterX=12.4 CenterY=14.3 CenterZ=0 NormalX=0 NormalY=0 NormalZ=1 AngleXU=0 Radius=0.9 StartAngle=3.14159 EndAngle=4.71239
    g4: LineSegment StartX=12.4 StartY=16.25 StartZ=0 EndX=16.7 EndY=16.25 EndZ=0
    g5: LineSegment StartX=17.6 StartY=15.35 StartZ=0 EndX=17.6 EndY=14.3 EndZ=0
    g6: LineSegment StartX=16.7 StartY=13.4 StartZ=0 EndX=12.4 EndY=13.4 EndZ=0
    g7: LineSegment StartX=11.5 StartY=14.3 StartZ=0 EndX=11.5 EndY=15.35 EndZ=0
  constraints (28):
    c: Coincident(g4,g0)
    c: Coincident(g4,g1)
    c: Horizontal(g4)
    c: Coincident(g5,g1)
    c: Coincident(g5,g2)
    c: Coincident(g6,g2)
    c: Coincident(g6,g3)
    c: Horizontal(g6)
    c: Coincident(g7,g3)
    c: Coincident(g7,g0)
    c: Vertical(g7)
    c: Radius(g0) = 0.9
    c: DistanceY(g0,g0) = 0
    c: Angle(g3) = 1.5708
    c: DistanceY(g3,g3) = 0
    c: DistanceY(g3,g0) = 1.05
    c: DistanceY(g3) = 14.3
    c: Radius(g3) = 0.9
    c: Radius(g2) = 0.9
    c: Radius(g1) = 0.9
    c: DistanceX(g6,g6) = 4.3
    c: DistanceX(g3) = 12.4
    c: DistanceY(g1,g1) = 0
    c: DistanceX(g2,g2) = 0
    c: Angle(g1) = 1.5708
    c: Angle(g2) = 1.5708
    c: Vertical(g5)
    c: DistanceX(g0,g0) = 0
FEATURE [Sketcher::SketchObject] Sketch015
  FullyConstrained = true
  Placement = pos=(0,0,0) rot=(1,0,0;1.5708rad)
  sketch-geometry (8):
    g0: ArcOfCircle CenterX=11.7 CenterY=15.45 CenterZ=0 NormalX=0 NormalY=0 NormalZ=1 AngleXU=0 Radius=0.9 StartAngle=1.5708 EndAngle=3.14159
    g1: ArcOfCircle CenterX=17.4 CenterY=15.45 CenterZ=0 NormalX=0 NormalY=0 NormalZ=1 AngleXU=0 Radius=0.9 StartAngle=4e-16 EndAngle=1.5708
    g2: ArcOfCircle CenterX=16.8 CenterY=14.2 CenterZ=0 NormalX=0 NormalY=0 NormalZ=1 AngleXU=0 Radius=1.5 StartAngle=4.71239 EndAngle=6.28319
    g3: ArcOfCircle CenterX=12.3 CenterY=14.2 CenterZ=0 NormalX=0 NormalY=0 NormalZ=1 AngleXU=0 Radius=1.5 StartAngle=3.14159 EndAngle=4.71239
    g4: LineSegment StartX=11.7 StartY=16.35 StartZ=0 EndX=17.4 EndY=16.35 EndZ=0
    g5: LineSegment StartX=18.3 StartY=15.45 StartZ=0 EndX=18.3 EndY=14.2 EndZ=0
    g6: LineSegment StartX=16.8 StartY=12.7 StartZ=0 EndX=12.3 EndY=12.7 EndZ=0
    g7: LineSegment StartX=10.8 StartY=14.2 StartZ=0 EndX=10.8 EndY=15.45 EndZ=0
  constraints (28):
    c: Coincident(g4,g0)
    c: Coincident(g4,g1)
    c: Horizontal(g4)
    c: Coincident(g5,g1)
    c: Coincident(g5,g2)
    c: Coincident(g6,g2)
    c: Coincident(g6,g3)
    c: Horizontal(g6)
    c: Coincident(g7,g3)
    c: Coincident(g7,g0)
    c: Vertical(g7)
    c: Radius(g0) = 0.9
    c: DistanceY(g0,g0) = 0
    c: Angle(g3) = 1.5708
    c: DistanceY(g3,g3) = 0
    c: DistanceY(g3,g0) = 1.25
    c: DistanceY(g3) = 14.2
    c: Radius(g3) = 1.5
    c: Radius(g2) = 1.5
    c: Radius(g1) = 0.9
    c: DistanceX(g6,g6) = 4.5
    c: DistanceX(g3) = 12.3
    c: DistanceY(g1,g1) = 0
    c: DistanceX(g2,g2) = 0
    c: Angle(g1) = 1.5708
    c: Angle(g2) = 1.5708
    c: Vertical(g5)
    c: DistanceX(g0,g0) = 0
FEATURE [Part::Extrusion] Extrude014
  Base = -> Sketch014
  Dir = (0,-1,-3e-16)
  DirMode = 2
  FaceMakerClass = Part::FaceMakerBullseye
  LengthFwd = 2.25
  LengthRev = 0
  Placement = pos=(0,2,0) rot=(0,0,1;0rad)
  Solid = true
  Symmetric = false
FEATURE [Part::Extrusion] Extrude015
  Base = -> Sketch015
  Dir = (0,-1,2e-16)
  DirMode = 2
  FaceMakerClass = Part::FaceMakerBullseye
  LengthFwd = 1
  LengthRev = 0
  Placement = pos=(0,3,0) rot=(0,0,1;0rad)
  Solid = true
  Symmetric = false
FEATURE [Part::MultiFuse] Fusion018  label="button1"
  Shapes = -> [Extrude014,Extrude015]
FEATURE [Part::MultiFuse] Fusion020  label="bottomCuts"
  Shapes = -> [Fusion017,Extrude011,Extrude004,Fusion007,Fusion001]
FEATURE [Part::Cut] Cut005  label="bottom005"
  Base = -> Fusion012
  Tool = -> Fusion020
FEATURE [Part::Fillet] Fillet006  label="batteryIndicator"
  Base = -> Cut005
  Edges = 4 edges r=0.25: [Edge178,Edge179,Edge180,Edge181]
FEATURE [Part::Fillet] Fillet007  label="buttons"
  Base = -> Fillet006
  Edges = 16 edges r=0.25: [Edge6,Edge7,Edge8,Edge9,Edge10,Edge11,Edge12,Edge13,Edge20,Edge21,Edge22,Edge23,Edge24,Edge25,Edge26,Edge27]
FEATURE [Part::Fillet] Fillet008  label="hdmi"
  Base = -> Fillet007
  Edges = 6 edges r=1: [Edge14,Edge15,Edge16,Edge17,Edge18,Edge19]
FEATURE [Part::Fillet] Fillet009  label="microUSB"
  Base = -> Fillet008
  Edges = 12 edges r=0.5: [Edge28,Edge29,Edge30,Edge31,Edge32,Edge33,Edge34,Edge35,Edge36,Edge37,Edge38,Edge39]
FEATURE [Part::Fillet] Fillet010  label="rest"
  Base = -> Fillet009
  Edges = 22 edges r=1: [Edge26,Edge27,Edge28,Edge29,Edge30,Edge31,Edge32,Edge33,Edge235,Edge236,Edge237,Edge238,Edge242,Edge243,Edge244,Edge274,Edge275,Edge276,Edge277,Edge397,Edge398,Edge399]
FEATURE [Part::Fillet] Fillet011  label="innerVents"
  Base = -> Fillet010
  Edges = 12 edges r=0.25: [Edge336,Edge341,Edge345,Edge349,Edge353,Edge357,Edge378,Edge382,Edge389,Edge390,Edge394,Edge398]
FEATURE [Part::Fillet] Fillet012  label="outerVents"
  Base = -> Fillet011
  Edges = 12 edges r=0.25: [Edge57,Edge117,Edge127,Edge137,Edge147,Edge157,Edge182,Edge186,Edge188,Edge194,Edge198,Edge202]
FEATURE [Part::Fillet] Fillet013  label="horVents"
  Base = -> Fillet012
  Edges = 24 edges r=0.25: [Edge6,Edge62,Edge72,Edge74,Edge78,Edge80,Edge84,Edge86,Edge90,Edge92,Edge96,Edge98,Edge215,Edge217,Edge228,Edge230,Edge234,Edge236,Edge240,Edge242,Edge246,Edge248,Edge252,Edge254]
FEATURE [Sketcher::SketchObject] Sketch016
  FullyConstrained = true
  Placement = pos=(0,0,0) rot=(1,0,0;1.5708rad)
  sketch-geometry (8):
    g0: ArcOfCircle CenterX=12.4 CenterY=15.35 CenterZ=0 NormalX=0 NormalY=0 NormalZ=1 AngleXU=0 Radius=0.9 StartAngle=1.5708 EndAngle=3.14159
    g1: ArcOfCircle CenterX=16.7 CenterY=15.35 CenterZ=0 NormalX=0 NormalY=0 NormalZ=1 AngleXU=0 Radius=0.9 StartAngle=9e-16 EndAngle=1.5708
    g2: ArcOfCircle CenterX=16.7 CenterY=14.3 CenterZ=0 NormalX=0 NormalY=0 NormalZ=1 AngleXU=0 Radius=0.9 StartAngle=4.71239 EndAngle=6.28319
    g3: ArcOfCircle CenterX=12.4 CenterY=14.3 CenterZ=0 NormalX=0 NormalY=0 NormalZ=1 AngleXU=0 Radius=0.9 StartAngle=3.14159 EndAngle=4.71239
    g4: LineSegment StartX=12.4 StartY=16.25 StartZ=0 EndX=16.7 EndY=16.25 EndZ=0
    g5: LineSegment StartX=17.6 StartY=15.35 StartZ=0 EndX=17.6 EndY=14.3 EndZ=0
    g6: LineSegment StartX=16.7 StartY=13.4 StartZ=0 EndX=12.4 EndY=13.4 EndZ=0
    g7: LineSegment StartX=11.5 StartY=14.3 StartZ=0 EndX=11.5 EndY=15.35 EndZ=0
  constraints (28):
    c: Coincident(g4,g0)
    c: Coincident(g4,g1)
    c: Horizontal(g4)
    c: Coincident(g5,g1)
    c: Coincident(g5,g2)
    c: Coincident(g6,g2)
    c: Coincident(g6,g3)
    c: Horizontal(g6)
    c: Coincident(g7,g3)
    c: Coincident(g7,g0)
    c: Vertical(g7)
    c: Radius(g0) = 0.9
    c: DistanceY(g0,g0) = 0
    c: Angle(g3) = 1.5708
    c: DistanceY(g3,g3) = 0
    c: DistanceY(g3,g0) = 1.05
    c: DistanceY(g3) = 14.3
    c: Radius(g3) = 0.9
    c: Radius(g2) = 0.9
    c: Radius(g1) = 0.9
    c: DistanceX(g6,g6) = 4.3
    c: DistanceX(g3) = 12.4
    c: DistanceY(g1,g1) = 0
    c: DistanceX(g2,g2) = 0
    c: Angle(g1) = 1.5708
    c: Angle(g2) = 1.5708
    c: Vertical(g5)
    c: DistanceX(g0,g0) = 0
FEATURE [Part::Extrusion] Extrude016
  Base = -> Sketch016
  Dir = (0,-1,-3e-16)
  DirMode = 2
  FaceMakerClass = Part::FaceMakerBullseye
  LengthFwd = 2.25
  LengthRev = 0
  Placement = pos=(0,2,0) rot=(0,0,1;0rad)
  Solid = true
  Symmetric = false
FEATURE [Sketcher::SketchObject] Sketch017
  FullyConstrained = true
  Placement = pos=(0,0,0) rot=(1,0,0;1.5708rad)
  sketch-geometry (8):
    g0: ArcOfCircle CenterX=11.7 CenterY=15.45 CenterZ=0 NormalX=0 NormalY=0 NormalZ=1 AngleXU=0 Radius=0.9 StartAngle=1.5708 EndAngle=3.14159
    g1: ArcOfCircle CenterX=17.4 CenterY=15.45 CenterZ=0 NormalX=0 NormalY=0 NormalZ=1 AngleXU=0 Radius=0.9 StartAngle=4e-16 EndAngle=1.5708
    g2: ArcOfCircle CenterX=16.8 CenterY=14.2 CenterZ=0 NormalX=0 NormalY=0 NormalZ=1 AngleXU=0 Radius=1.5 StartAngle=4.71239 EndAngle=6.28319
    g3: ArcOfCircle CenterX=12.3 CenterY=14.2 CenterZ=0 NormalX=0 NormalY=0 NormalZ=1 AngleXU=0 Radius=1.5 StartAngle=3.14159 EndAngle=4.71239
    g4: LineSegment StartX=11.7 StartY=16.35 StartZ=0 EndX=17.4 EndY=16.35 EndZ=0
    g5: LineSegment StartX=18.3 StartY=15.45 StartZ=0 EndX=18.3 EndY=14.2 EndZ=0
    g6: LineSegment StartX=16.8 StartY=12.7 StartZ=0 EndX=12.3 EndY=12.7 EndZ=0
    g7: LineSegment StartX=10.8 StartY=14.2 StartZ=0 EndX=10.8 EndY=15.45 EndZ=0
  constraints (28):
    c: Coincident(g4,g0)
    c: Coincident(g4,g1)
    c: Horizontal(g4)
    c: Coincident(g5,g1)
    c: Coincident(g5,g2)
    c: Coincident(g6,g2)
    c: Coincident(g6,g3)
    c: Horizontal(g6)
    c: Coincident(g7,g3)
    c: Coincident(g7,g0)
    c: Vertical(g7)
    c: Radius(g0) = 0.9
    c: DistanceY(g0,g0) = 0
    c: Angle(g3) = 1.5708
    c: DistanceY(g3,g3) = 0
    c: DistanceY(g3,g0) = 1.25
    c: DistanceY(g3) = 14.2
    c: Radius(g3) = 1.5
    c: Radius(g2) = 1.5
    c: Radius(g1) = 0.9
    c: DistanceX(g6,g6) = 4.5
    c: DistanceX(g3) = 12.3
    c: DistanceY(g1,g1) = 0
    c: DistanceX(g2,g2) = 0
    c: Angle(g1) = 1.5708
    c: Angle(g2) = 1.5708
    c: Vertical(g5)
    c: DistanceX(g0,g0) = 0
FEATURE [Part::Extrusion] Extrude017
  Base = -> Sketch017
  Dir = (0,-1,2e-16)
  DirMode = 2
  FaceMakerClass = Part::FaceMakerBullseye
  LengthFwd = 1
  LengthRev = 0
  Placement = pos=(0,3,0) rot=(0,0,1;0rad)
  Solid = true
  Symmetric = false
FEATURE [Part::MultiFuse] Fusion021  label="button002"
  Shapes = -> [Extrude016,Extrude017]
